FREECAD ASSEMBLY — COMPONENT RECIPES ("MainAssembly")

This assembly document has 21 components, labeled P0..P20 below (a component is one placed body or linked part). 10 of them carry a construction recipe — the FreeCAD feature program that regenerates the part from scratch, quoted from this document or its linked companion documents; the rest are supplied as boundary geometry only. No exploded tour is included for this assembly.
COMPONENT P0 — recipe-attached ("AxleHolderPart", a linked part whose construction recipe lives in a companion FreeCAD document of the same project; that document's serialized recipe follows).
Construction recipe (the companion document, serialized — sketch geometry with constraints, then the solid features built on it; lengths are millimeters unless a unit is written):

FCSTD DOCUMENT  (FreeCAD 1.0R39109 (Git))
Label: AxleHolder
License: All rights reserved
LicenseURL: https://en.wikipedia.org/wiki/All_rights_reserved
objects: Sketcher::SketchObject×2, PartDesign::Pad×2, PartDesign::Body×1, App::Part×1
note: 11 computed .brp shape members not serialized (recipe doc carries the construction recipe); baked Part::Feature solids carry a one-line shape summary decoded from their .brp

FEATURE [Sketcher::SketchObject] Sketch
  ArcFitTolerance = 1e-06
  AttachmentSupport = -> [XY_Plane001]
  FullyConstrained = true
  MakeInternals = false
  MapMode = 5
  sketch-geometry (6):
    g0: LineSegment StartX=-7.3 StartY=-4.3 StartZ=0 EndX=7.3 EndY=-4.3 EndZ=0
    g1: LineSegment StartX=7.3 StartY=-4.3 StartZ=0 EndX=7.3 EndY=4.3 EndZ=0
    g2: LineSegment StartX=7.3 StartY=4.3 StartZ=0 EndX=-7.3 EndY=4.3 EndZ=0
    g3: LineSegment StartX=-7.3 StartY=4.3 StartZ=0 EndX=-7.3 EndY=-4.3 EndZ=0
    g4: GeomPoint [constr] X=0 Y=0 Z=0
    g5: Circle CenterX=0 CenterY=0 CenterZ=0 NormalX=0 NormalY=0 NormalZ=1 AngleXU=0 Radius=3.2
  constraints (14):
    c: Coincident(g0,g1)
    c: Coincident(g1,g2)
    c: Coincident(g2,g3)
    c: Coincident(g3,g0)
    c: Horizontal(g0)
    c: Horizontal(g2)
    c: Vertical(g1)
    c: Vertical(g3)
    c: Symmetric(g2,g0,g4)
    c: Distance(g1,g3) = 14.6
    c: Distance(g0,g2) = 8.6
    c: Coincident(g4,g-1)
    c: Diameter(g5) = 6.4
    c: Coincident(g5,g4)
FEATURE [PartDesign::Pad] Pad
  Direction = (0,0,1)
  Length = 2.6
  Length2 = 10
  Profile = -> Sketch
  ReferenceAxis = -> Sketch [N_Axis]
  Refine = true
  Suppressed = false
  Type = 0
FEATURE [Sketcher::SketchObject] Sketch001
  ArcFitTolerance = 1e-06
  AttachmentSupport = -> [Pad]
  ExternalGeometry = -> [Sketch]
  FullyConstrained = true
  MakeInternals = false
  MapMode = 5
  Placement = pos=(0,0,2.6) rot=(0,0,1;0rad)
  sketch-geometry (6):
    g0: Circle CenterX=0 CenterY=0 CenterZ=0 NormalX=0 NormalY=0 NormalZ=1 AngleXU=0 Radius=3.2
    g1: LineSegment StartX=-4.3 StartY=-4.3 StartZ=0 EndX=4.3 EndY=-4.3 EndZ=0
    g2: LineSegment StartX=4.3 StartY=-4.3 StartZ=0 EndX=4.3 EndY=4.3 EndZ=0
    g3: LineSegment StartX=4.3 StartY=4.3 StartZ=0 EndX=-4.3 EndY=4.3 EndZ=0
    g4: LineSegment StartX=-4.3 StartY=4.3 StartZ=0 EndX=-4.3 EndY=-4.3 EndZ=0
    g5: GeomPoint [constr] X=0 Y=0 Z=0
  constraints (14):
    c: Coincident(g0,g-1)
    c: Equal(g0,g-3)
    c: Coincident(g1,g2)
    c: Coincident(g2,g3)
    c: Coincident(g3,g4)
    c: Coincident(g4,g1)
    c: Horizontal(g1)
    c: Horizontal(g3)
    c: Vertical(g2)
    c: Vertical(g4)
    c: Symmetric(g3,g1,g5)
    c: Coincident(g5,g0)
    c: PointOnObject(g2,g-4)
    c: Equal(g3,g2)
FEATURE [PartDesign::Pad] Pad001
  BaseFeature = -> Pad
  Direction = (0,0,1)
  Length = 4.4
  Length2 = 10
  Profile = -> Sketch001
  ReferenceAxis = -> Sketch001 [N_Axis]
  Refine = true
  Suppressed = false
  Type = 0
FEATURE [PartDesign::Body] Body  label="AxleHolderBody"
  AllowCompound = false
  Group = -> [Sketch,Pad,Sketch001,Pad001]
  Origin = -> Origin001
  Tip = -> Pad001
FEATURE [App::Part] Part  label="AxleHolderPart"
  Group = -> [Body]
  Origin = -> Origin
COMPONENT P1 — same part as P0; its construction recipe is shown at P0.
COMPONENT P2 — same part as P0; its construction recipe is shown at P0.
COMPONENT P3 — geometry summary ("BackWheelAxlePart"; no construction recipe available for this part):
  bounding box: 39.9 x 14.0 x 14.0 mm
  tessellated surface: 2,774 triangles
  volume: 1874 mm^3 (24% of its bounding box)
  symmetry: 2-fold rotationally symmetric about the x axis
COMPONENT P4 — geometry summary ("BackWheelAxlePart001"; no construction recipe available for this part):
  bounding box: 39.9 x 14.0 x 14.0 mm
  tessellated surface: 2,774 triangles
  volume: 1874 mm^3 (24% of its bounding box)
  symmetry: 2-fold rotationally symmetric about the x axis
COMPONENT P5 — geometry summary ("BackWheelConnectorPart"; no construction recipe available for this part):
  bounding box: 23.7 x 23.7 x 20.0 mm
  tessellated surface: 5,512 triangles
  volume: 2183 mm^3 (19% of its bounding box)
COMPONENT P6 — geometry summary ("BackWheelConnectorPart001"; no construction recipe available for this part):
  bounding box: 23.7 x 23.7 x 20.0 mm
  tessellated surface: 5,512 triangles
  volume: 2183 mm^3 (19% of its bounding box)
COMPONENT P7 — geometry summary ("BackWheelStopperPart"; no construction recipe available for this part):
  bounding box: 28.0 x 15.0 x 3.6 mm
  tessellated surface: 2,928 triangles
  volume: 623 mm^3 (41% of its bounding box)
  symmetry: 2-fold rotationally symmetric about the x axis; mirror-symmetric across its y mid-plane, z mid-plane
COMPONENT P8 — geometry summary ("BackWheelStopperPart001"; no construction recipe available for this part):
  bounding box: 28.0 x 15.0 x 3.6 mm
  tessellated surface: 2,928 triangles
  volume: 623 mm^3 (41% of its bounding box)
  symmetry: 2-fold rotationally symmetric about the x axis; mirror-symmetric across its y mid-plane, z mid-plane
COMPONENT P9 — recipe-attached ("ChassisPart", a linked part whose construction recipe lives in a companion FreeCAD document of the same project; that document's serialized recipe follows).
Construction recipe (the companion document, serialized — sketch geometry with constraints, then the solid features built on it; lengths are millimeters unless a unit is written):

FCSTD DOCUMENT  (FreeCAD 1.0R39319 (Git))
Label: Chassis
License: All rights reserved
LicenseURL: https://en.wikipedia.org/wiki/All_rights_reserved
objects: Sketcher::SketchObject×18, PartDesign::Pocket×11, PartDesign::Pad×7, PartDesign::Fillet×2, App::Link×1, PartDesign::SubShapeBinder×1, PartDesign::Body×1, App::Part×1
note: 98 computed .brp shape members not serialized (recipe doc carries the construction recipe); baked Part::Feature solids carry a one-line shape summary decoded from their .brp
EXTERNAL_REF file=../Models/SteeringAckermannModel.FCStd obj=Spreadsheet
EXTERNAL_REF file=../Models/SteeringAckermannModel.FCStd obj=Part

FEATURE [App::Link] Link  label="SteeringAckermannSpreadsheet"
  LinkedObject = -> <external ../Models/SteeringAckermannModel.FCStd>#Spreadsheet
FEATURE [PartDesign::SubShapeBinder] Binder  label="SteeringAckermannModel"
  BindCopyOnChange = 0
  BindMode = 0
  ClaimChildren = false
  Context = -> Part [Body.Binder.]
  Fuse = false
  MakeFace = true
  OffsetFill = false
  OffsetIntersection = false
  OffsetJoinType = 0
  OffsetOpenResult = false
  PartialLoad = false
  Refine = true
  Relative = true
  Support = -> [<external ../Models/SteeringAckermannModel.FCStd>#Part[Sketch001.]]
  _Version = 2
FEATURE [Sketcher::SketchObject] Sketch
  ArcFitTolerance = 1e-06
  AttachmentSupport = -> [XY_Plane001]
  ExternalGeometry = -> [Binder]
  FullyConstrained = true
  MakeInternals = false
  MapMode = 5
  expr: Constraints[31] = <<SteeringAckermannSpreadsheet>>.wheeldepth / 2 + 4
  expr: Constraints[33] = <<SteeringAckermannSpreadsheet>>.wheeldia / 2 + 2
  expr: Constraints[34] = <<SteeringAckermannSpreadsheet>>.wheeldia / 2
  expr: Constraints[43] = <<SteeringAckermannSpreadsheet>>.bodywidth
  sketch-geometry (22):
    g0: LineSegment StartX=-26 StartY=4 StartZ=0 EndX=-26 EndY=-4 EndZ=0
    g1: LineSegment StartX=-26 StartY=4 StartZ=0 EndX=-10 EndY=22 EndZ=0
    g2: LineSegment StartX=-10 StartY=22 StartZ=0 EndX=10 EndY=22 EndZ=0
    g3: LineSegment StartX=-26 StartY=-4 StartZ=0 EndX=-14 EndY=-13 EndZ=0
    g4: LineSegment StartX=-14 StartY=-13 StartZ=0 EndX=-14 EndY=-41 EndZ=0
    g5: LineSegment StartX=10 StartY=22 StartZ=0 EndX=26 EndY=4 EndZ=0
    g6: LineSegment StartX=26 StartY=4 StartZ=0 EndX=26 EndY=-4 EndZ=0
    g7: LineSegment StartX=26 StartY=-4 StartZ=0 EndX=14 EndY=-13 EndZ=0
    g8: LineSegment StartX=14 StartY=-13 StartZ=0 EndX=14 EndY=-41 EndZ=0
    g9: LineSegment StartX=-14 StartY=-41 StartZ=0 EndX=-60 EndY=-41 EndZ=0
    g10: LineSegment StartX=-60 StartY=-41 StartZ=0 EndX=-60 EndY=-164 EndZ=0
    g11: LineSegment StartX=-60 StartY=-164 StartZ=0 EndX=-32 EndY=-164 EndZ=0
    g12: LineSegment StartX=-32 StartY=-164 StartZ=0 EndX=-32 EndY=-222 EndZ=0
    g13: LineSegment StartX=-32 StartY=-222 StartZ=0 EndX=32 EndY=-222 EndZ=0
    g14: LineSegment StartX=14 StartY=-41 StartZ=0 EndX=60 EndY=-41 EndZ=0
    g15: LineSegment StartX=60 StartY=-41 StartZ=0 EndX=60 EndY=-164 EndZ=0
    g16: LineSegment StartX=60 StartY=-164 StartZ=0 EndX=32 EndY=-164 EndZ=0
    g17: LineSegment StartX=32 StartY=-164 StartZ=0 EndX=32 EndY=-222 EndZ=0
    g18: Circle CenterX=-22 CenterY=0 CenterZ=0 NormalX=0 NormalY=0 NormalZ=1 AngleXU=0 Radius=1.5
    g19: Circle CenterX=22 CenterY=0 CenterZ=0 NormalX=0 NormalY=0 NormalZ=1 AngleXU=0 Radius=1.5
    g20: Circle CenterX=-11.3195 CenterY=16 CenterZ=0 NormalX=0 NormalY=0 NormalZ=1 AngleXU=0 Radius=1.5
    g21: Circle CenterX=11.3195 CenterY=16 CenterZ=0 NormalX=0 NormalY=0 NormalZ=1 AngleXU=0 Radius=1.5
  constraints (54):
    c: Distance(g0,g0) = 8
    c: Symmetric(g0,g0,g-1)
    c: Distance(g-3,g0) = 8
    c: Coincident(g1,g0)
    c: Coincident(g2,g1)
    c: DistanceX(g2,g2) = 20
    c: Distance(g-1,g2) = 22
    c: Symmetric(g1,g2,g-2)
    c: Coincident(g3,g0)
    c: Coincident(g4,g3)
    c: Vertical(g4)
    c: DistanceY(g4,g4) = 28
    c: Coincident(g5,g2)
    c: Coincident(g6,g5)
    c: Coincident(g7,g6)
    c: Coincident(g8,g7)
    c: Symmetric(g0,g5,g-2)
    c: Symmetric(g0,g6,g-2)
    c: Symmetric(g3,g7,g-2)
    c: Symmetric(g4,g8,g-2)
    c: Distance(g8,g4) = 28
    c: Coincident(g9,g4)
    c: Horizontal(g9)
    c: Coincident(g10,g9)
    c: Vertical(g10)
    c: Coincident(g11,g10)
    c: Horizontal(g11)
    c: Coincident(g12,g11)
    c: Vertical(g12)
    c: Coincident(g13,g12)
    c: DistanceY(g10,g10) = 123
    c: Distance(g-5,g12) = 16
    c: Symmetric(g12,g13,g-2)
    c: DistanceY(g-7,g11) = 30
    c: DistanceY(g12,g-7) = 28
    c: Coincident(g14,g8)
    c: Coincident(g15,g14)
    c: Coincident(g16,g15)
    c: Coincident(g17,g16)
    c: Coincident(g17,g13)
    c: Symmetric(g9,g14,g-2)
    c: Symmetric(g10,g15,g-2)
    c: Symmetric(g11,g16,g-2)
    c: Distance(g15,g10) = 120
    c: Diameter(g18) = 3
    c: PointOnObject(g18,g-1)
    c: Distance(g18,g0) = 4
    c: Symmetric(g18,g19,g-2)
    c: Diameter(g20) = 3
    c: Equal(g18,g19)
    c: Distance(g20,g1) = 3
    c: DistanceY(g20,g1) = 6
    c: Symmetric(g20,g21,g-2)
    c: Equal(g20,g21)
FEATURE [PartDesign::Pad] Pad
  Direction = (0,0,1)
  Length = 8
  Length2 = 10
  Profile = -> Sketch
  ReferenceAxis = -> Sketch [N_Axis]
  Refine = true
  Suppressed = false
  Type = 0
FEATURE [Sketcher::SketchObject] Sketch001
  ArcFitTolerance = 1e-06
  AttachmentSupport = -> [Pad]
  ExternalGeometry = -> [Sketch]
  FullyConstrained = true
  MakeInternals = false
  MapMode = 5
  Placement = pos=(0,0,8) rot=(0,0,1;0rad)
  sketch-geometry (16):
    g0: LineSegment StartX=-26 StartY=-4 StartZ=0 EndX=-26 EndY=4 EndZ=0
    g1: LineSegment StartX=-26 StartY=4 StartZ=0 EndX=-10 EndY=22 EndZ=0
    g2: LineSegment StartX=10 StartY=22 StartZ=0 EndX=26 EndY=4 EndZ=0
    g3: LineSegment StartX=26 StartY=4 StartZ=0 EndX=26 EndY=-4 EndZ=0
    g4: Circle CenterX=-22 CenterY=0 CenterZ=0 NormalX=0 NormalY=0 NormalZ=1 AngleXU=0 Radius=1.5
    g5: Circle CenterX=-11.3195 CenterY=16 CenterZ=0 NormalX=0 NormalY=0 NormalZ=1 AngleXU=0 Radius=1.5
    g6: Circle CenterX=11.3195 CenterY=16 CenterZ=0 NormalX=0 NormalY=0 NormalZ=1 AngleXU=0 Radius=1.5
    g7: Circle CenterX=22 CenterY=0 CenterZ=0 NormalX=0 NormalY=0 NormalZ=1 AngleXU=0 Radius=1.5
    g8: LineSegment StartX=-10 StartY=22 StartZ=0 EndX=-8 EndY=22 EndZ=0
    g9: LineSegment StartX=-26 StartY=-4 StartZ=0 EndX=-11.3 EndY=-4 EndZ=0
    g10: LineSegment StartX=-11.3 StartY=-4 StartZ=0 EndX=-8 EndY=-2.75 EndZ=0
    g11: LineSegment StartX=-8 StartY=22 StartZ=0 EndX=-8 EndY=-2.75 EndZ=0
    g12: LineSegment StartX=10 StartY=22 StartZ=0 EndX=8 EndY=22 EndZ=0
    g13: LineSegment StartX=8 StartY=22 StartZ=0 EndX=8 EndY=-2.75 EndZ=0
    g14: LineSegment StartX=8 StartY=-2.75 StartZ=0 EndX=11.3 EndY=-4 EndZ=0
    g15: LineSegment StartX=11.3 StartY=-4 StartZ=0 EndX=26 EndY=-4 EndZ=0
  constraints (35):
    c: Coincident(g0,g-4)
    c: Coincident(g0,g-5)
    c: Coincident(g1,g0)
    c: Coincident(g1,g-6)
    c: Coincident(g2,g-8)
    c: Coincident(g3,g2)
    c: Coincident(g3,g-8)
    c: Coincident(g4,g-3)
    c: Equal(g4,g-3)
    c: Coincident(g5,g-9)
    c: Equal(g5,g-9)
    c: Coincident(g6,g-10)
    c: Equal(g6,g-10)
    c: Coincident(g7,g-11)
    c: Equal(g7,g-11)
    c: Coincident(g2,g-7)
    c: Coincident(g8,g1)
    c: PointOnObject(g8,g-6)
    c: Coincident(g9,g0)
    c: Horizontal(g9)
    c: Coincident(g10,g9)
    c: Coincident(g11,g8)
    c: Coincident(g11,g10)
    c: Vertical(g11)
    c: DistanceY(g11,g11) = 24.75
    c: DistanceX(g9,g9) = 14.7
    c: Coincident(g12,g2)
    c: Coincident(g13,g12)
    c: Coincident(g14,g13)
    c: Coincident(g15,g14)
    c: Coincident(g15,g3)
    c: Symmetric(g8,g12,g-2)
    c: Symmetric(g10,g13,g-2)
    c: Symmetric(g9,g14,g-2)
    c: DistanceX(g10,g13) = 16
FEATURE [PartDesign::Pad] Pad001
  BaseFeature = -> Pad
  Direction = (0,0,1)
  Length = 5.5
  Length2 = 10
  Profile = -> Sketch001
  ReferenceAxis = -> Sketch001 [N_Axis]
  Refine = true
  Suppressed = false
  Type = 0
  expr: Length = <<SteeringAckermannSpreadsheet>>.wheeldia / 2 - 8 - 8 - 3 - 7 / 2
FEATURE [Sketcher::SketchObject] Sketch002
  ArcFitTolerance = 1e-06
  AttachmentSupport = -> [Pad001]
  ExternalGeometry = -> [Sketch001,Binder]
  FullyConstrained = true
  MakeInternals = false
  MapMode = 5
  Placement = pos=(0,0,13.5) rot=(0,0,1;0rad)
  sketch-geometry (22):
    g0: LineSegment StartX=-26 StartY=4 StartZ=0 EndX=-10 EndY=22 EndZ=0
    g1: LineSegment StartX=-10 StartY=22 StartZ=0 EndX=-8 EndY=22 EndZ=0
    g2: LineSegment StartX=-8 StartY=22 StartZ=0 EndX=-8 EndY=-2.75 EndZ=0
    g3: LineSegment StartX=-8 StartY=-2.75 StartZ=0 EndX=-11.3 EndY=-4 EndZ=0
    g4: LineSegment StartX=-11.3 StartY=-4 StartZ=0 EndX=-26 EndY=-4 EndZ=0
    g5: LineSegment StartX=26 StartY=4 StartZ=0 EndX=10 EndY=22 EndZ=0
    g6: LineSegment StartX=10 StartY=22 StartZ=0 EndX=8 EndY=22 EndZ=0
    g7: LineSegment StartX=8 StartY=22 StartZ=0 EndX=8 EndY=-2.75 EndZ=0
    g8: LineSegment StartX=8 StartY=-2.75 StartZ=0 EndX=11.3 EndY=-4 EndZ=0
    g9: LineSegment StartX=11.3 StartY=-4 StartZ=0 EndX=26 EndY=-4 EndZ=0
    g10: Circle CenterX=-22 CenterY=0 CenterZ=0 NormalX=0 NormalY=0 NormalZ=1 AngleXU=0 Radius=1.5
    g11: Circle CenterX=-11.3195 CenterY=16 CenterZ=0 NormalX=0 NormalY=0 NormalZ=1 AngleXU=0 Radius=1.5
    g12: Circle CenterX=22 CenterY=0 CenterZ=0 NormalX=0 NormalY=0 NormalZ=1 AngleXU=0 Radius=1.5
    g13: Circle CenterX=11.3195 CenterY=16 CenterZ=0 NormalX=0 NormalY=0 NormalZ=1 AngleXU=0 Radius=1.5
    g14: Circle CenterX=-34 CenterY=0 CenterZ=0 NormalX=0 NormalY=0 NormalZ=1 AngleXU=0 Radius=1.5
    g15: Circle CenterX=34 CenterY=0 CenterZ=0 NormalX=0 NormalY=0 NormalZ=1 AngleXU=0 Radius=1.5
    g16: ArcOfCircle CenterX=-34 CenterY=0 CenterZ=0 NormalX=0 NormalY=0 NormalZ=1 AngleXU=0 Radius=4 StartAngle=1.5708 EndAngle=4.71239
    g17: LineSegment StartX=-26 StartY=-4 StartZ=0 EndX=-34 EndY=-4 EndZ=0
    g18: LineSegment StartX=-26 StartY=4 StartZ=0 EndX=-34 EndY=4 EndZ=0
    g19: ArcOfCircle CenterX=34 CenterY=0 CenterZ=0 NormalX=0 NormalY=0 NormalZ=1 AngleXU=0 Radius=4 StartAngle=4.71239 EndAngle=7.85398
    g20: LineSegment StartX=26 StartY=-4 StartZ=0 EndX=34 EndY=-4 EndZ=0
    g21: LineSegment StartX=26 StartY=4 StartZ=0 EndX=34 EndY=4 EndZ=0
  constraints (44):
    c: Coincident(g0,g-3)
    c: Coincident(g0,g-4)
    c: Coincident(g1,g0)
    c: Coincident(g1,g-5)
    c: Coincident(g2,g1)
    c: Coincident(g2,g-6)
    c: Coincident(g3,g2)
    c: Coincident(g3,g-7)
    c: Coincident(g4,g3)
    c: Coincident(g4,g-7)
    c: Coincident(g5,g-12)
    c: Coincident(g5,g-12)
    c: Coincident(g6,g5)
    c: Coincident(g6,g-11)
    c: Coincident(g7,g6)
    c: Coincident(g7,g-13)
    c: Coincident(g8,g7)
    c: Coincident(g8,g-14)
    c: Coincident(g9,g8)
    c: Coincident(g9,g-14)
    c: Coincident(g10,g-8)
    c: Equal(g10,g-8)
    c: Coincident(g11,g-9)
    c: Equal(g11,g-9)
    c: Coincident(g12,g-15)
    c: Equal(g12,g-15)
    c: Coincident(g13,g-16)
    c: Equal(g13,g-16)
    c: Diameter(g14) = 3
    c: Coincident(g14,g-17)
    c: Coincident(g15,g-18)
    c: Equal(g14,g15)
    c: Coincident(g16,g14)
    c: Coincident(g17,g4)
    c: Coincident(g18,g0)
    c: Tangent(g18,g16) = -1.5708
    c: Tangent(g17,g16) = 1.5708
    c: Horizontal(g17)
    c: Coincident(g19,g15)
    c: Coincident(g20,g9)
    c: Coincident(g21,g5)
    c: Tangent(g20,g19) = -1.5708
    c: Tangent(g21,g19) = 1.5708
    c: Horizontal(g20)
FEATURE [PartDesign::Pad] Pad002
  BaseFeature = -> Pad001
  Direction = (0,0,1)
  Length = 3
  Length2 = 10
  Profile = -> Sketch002
  ReferenceAxis = -> Sketch002 [N_Axis]
  Refine = true
  Suppressed = false
  Type = 0
FEATURE [Sketcher::SketchObject] Sketch003
  ArcFitTolerance = 1e-06
  AttachmentSupport = -> [Pad002]
  ExternalGeometry = -> [Sketch]
  FullyConstrained = true
  MakeInternals = false
  MapMode = 5
  Placement = pos=(0,0,16.5) rot=(0,0,1;0rad)
  expr: Constraints[24] = Sketch001.Constraints[24]
  expr: Constraints[25] = Sketch001.Constraints[25]
  expr: Constraints[34] = Sketch001.Constraints[34]
  sketch-geometry (16):
    g0: LineSegment StartX=-26 StartY=-4 StartZ=0 EndX=-26 EndY=4 EndZ=0
    g1: LineSegment StartX=-26 StartY=4 StartZ=0 EndX=-10 EndY=22 EndZ=0
    g2: LineSegment StartX=10 StartY=22 StartZ=0 EndX=26 EndY=4 EndZ=0
    g3: LineSegment StartX=26 StartY=4 StartZ=0 EndX=26 EndY=-4 EndZ=0
    g4: Circle CenterX=-22 CenterY=0 CenterZ=0 NormalX=0 NormalY=0 NormalZ=1 AngleXU=0 Radius=1.5
    g5: Circle CenterX=-11.3195 CenterY=16 CenterZ=0 NormalX=0 NormalY=0 NormalZ=1 AngleXU=0 Radius=1.5
    g6: Circle CenterX=11.3195 CenterY=16 CenterZ=0 NormalX=0 NormalY=0 NormalZ=1 AngleXU=0 Radius=1.5
    g7: Circle CenterX=22 CenterY=0 CenterZ=0 NormalX=0 NormalY=0 NormalZ=1 AngleXU=0 Radius=1.5
    g8: LineSegment StartX=-10 StartY=22 StartZ=0 EndX=-8 EndY=22 EndZ=0
    g9: LineSegment StartX=-26 StartY=-4 StartZ=0 EndX=-11.3 EndY=-4 EndZ=0
    g10: LineSegment StartX=-11.3 StartY=-4 StartZ=0 EndX=-8 EndY=-2.75 EndZ=0
    g11: LineSegment StartX=-8 StartY=22 StartZ=0 EndX=-8 EndY=-2.75 EndZ=0
    g12: LineSegment StartX=10 StartY=22 StartZ=0 EndX=8 EndY=22 EndZ=0
    g13: LineSegment StartX=8 StartY=22 StartZ=0 EndX=8 EndY=-2.75 EndZ=0
    g14: LineSegment StartX=8 StartY=-2.75 StartZ=0 EndX=11.3 EndY=-4 EndZ=0
    g15: LineSegment StartX=11.3 StartY=-4 StartZ=0 EndX=26 EndY=-4 EndZ=0
  constraints (35):
    c: Coincident(g0,g-4)
    c: Coincident(g0,g-5)
    c: Coincident(g1,g0)
    c: Coincident(g1,g-6)
    c: Coincident(g2,g-8)
    c: Coincident(g3,g2)
    c: Coincident(g3,g-8)
    c: Coincident(g4,g-3)
    c: Equal(g4,g-3)
    c: Coincident(g5,g-9)
    c: Equal(g5,g-9)
    c: Coincident(g6,g-10)
    c: Equal(g6,g-10)
    c: Coincident(g7,g-11)
    c: Equal(g7,g-11)
    c: Coincident(g2,g-7)
    c: Coincident(g8,g1)
    c: PointOnObject(g8,g-6)
    c: Coincident(g9,g0)
    c: Horizontal(g9)
    c: Coincident(g10,g9)
    c: Coincident(g11,g8)
    c: Coincident(g11,g10)
    c: Vertical(g11)
    c: DistanceY(g11,g11) = 24.75
    c: DistanceX(g9,g9) = 14.7
    c: Coincident(g12,g2)
    c: Coincident(g13,g12)
    c: Coincident(g14,g13)
    c: Coincident(g15,g14)
    c: Coincident(g15,g3)
    c: Symmetric(g8,g12,g-2)
    c: Symmetric(g10,g13,g-2)
    c: Symmetric(g9,g14,g-2)
    c: DistanceX(g10,g13) = 16
FEATURE [PartDesign::Pad] Pad003
  BaseFeature = -> Pad002
  Direction = (0,0,1)
  Length = 7
  Length2 = 10
  Profile = -> Sketch003
  ReferenceAxis = -> Sketch003 [N_Axis]
  Refine = true
  Suppressed = false
  Type = 0
FEATURE [Sketcher::SketchObject] Sketch004
  ArcFitTolerance = 1e-06
  AttachmentSupport = -> [Pad003]
  ExternalGeometry = -> [Binder,Pad003]
  FullyConstrained = true
  MakeInternals = false
  MapMode = 5
  Placement = pos=(0,0,8) rot=(0,0,1;0rad)
  sketch-geometry (14):
    g0: LineSegment StartX=-23 StartY=-179 StartZ=0 EndX=-23 EndY=-209 EndZ=0
    g1: LineSegment [constr] StartX=-23 StartY=-209 StartZ=0 EndX=-16 EndY=-209 EndZ=0
    g2: LineSegment StartX=-16 StartY=-209 StartZ=0 EndX=-16 EndY=-179 EndZ=0
    g3: LineSegment StartX=-16 StartY=-179 StartZ=0 EndX=-23 EndY=-179 EndZ=0
    g4: LineSegment StartX=-23 StartY=-222 StartZ=0 EndX=-16 EndY=-222 EndZ=0
    g5: LineSegment StartX=-23 StartY=-222 StartZ=0 EndX=-23 EndY=-209 EndZ=0
    g6: LineSegment StartX=-16 StartY=-222 StartZ=0 EndX=-16 EndY=-209 EndZ=0
    g7: LineSegment StartX=23 StartY=-179 StartZ=0 EndX=23 EndY=-209 EndZ=0
    g8: LineSegment [constr] StartX=23 StartY=-209 StartZ=0 EndX=16 EndY=-209 EndZ=0
    g9: LineSegment StartX=16 StartY=-209 StartZ=0 EndX=16 EndY=-179 EndZ=0
    g10: LineSegment StartX=16 StartY=-179 StartZ=0 EndX=23 EndY=-179 EndZ=0
    g11: LineSegment StartX=23 StartY=-222 StartZ=0 EndX=16 EndY=-222 EndZ=0
    g12: LineSegment StartX=23 StartY=-222 StartZ=0 EndX=23 EndY=-209 EndZ=0
    g13: LineSegment StartX=16 StartY=-222 StartZ=0 EndX=16 EndY=-209 EndZ=0
  constraints (33):
    c: Coincident(g0,g1)
    c: Coincident(g1,g2)
    c: Coincident(g2,g3)
    c: Coincident(g3,g0)
    c: Vertical(g2)
    c: Horizontal(g1)
    c: Horizontal(g3)
    c: Symmetric(g0,g0,g-3)
    c: PointOnObject(g4,g-4)
    c: PointOnObject(g4,g-4)
    c: Coincident(g5,g4)
    c: Coincident(g5,g0)
    c: Vertical(g5)
    c: Coincident(g6,g4)
    c: Coincident(g6,g1)
    c: Vertical(g6)
    c: DistanceY(g0,g0) = 30
    c: DistanceX(g3,g3) = 7
    c: Coincident(g7,g8)
    c: Coincident(g8,g9)
    c: Coincident(g9,g10)
    c: Coincident(g10,g7)
    c: Coincident(g12,g11)
    c: Coincident(g12,g7)
    c: Coincident(g13,g11)
    c: Coincident(g13,g8)
    c: Symmetric(g4,g11,g-2)
    c: Symmetric(g4,g11,g-2)
    c: Symmetric(g1,g8,g-2)
    c: Symmetric(g0,g7,g-2)
    c: Symmetric(g2,g9,g-2)
    c: Symmetric(g0,g7,g-2)
    c: DistanceX(g2,g9) = 32
FEATURE [PartDesign::Pad] Pad004
  BaseFeature = -> Pad003
  Direction = (0,0,1)
  Length = 51
  Length2 = 10
  Profile = -> Sketch004
  ReferenceAxis = -> Sketch004 [N_Axis]
  Refine = true
  Suppressed = false
  Type = 0
FEATURE [Sketcher::SketchObject] Sketch005
  ArcFitTolerance = 1e-06
  AttachmentSupport = -> [Pad004]
  ExternalGeometry = -> [Pad004,Sketch004]
  FullyConstrained = true
  MakeInternals = false
  MapMode = 5
  Placement = pos=(-23,0,0) rot=(0.57735,-0.57735,-0.57735;2.0944rad)
  expr: Constraints[3] = <<SteeringAckermannSpreadsheet>>.wheeldia / 2 - 8 - 8 + 24 / 2
  sketch-geometry (12):
    g0: LineSegment [constr] StartX=194 StartY=59 StartZ=0 EndX=194 EndY=8 EndZ=0
    g1: LineSegment [constr] StartX=179 StartY=32 StartZ=0 EndX=222 EndY=32 EndZ=0
    g2: LineSegment StartX=186.5 StartY=15.5 StartZ=0 EndX=201.5 EndY=15.5 EndZ=0
    g3: LineSegment StartX=201.5 StartY=15.5 StartZ=0 EndX=201.5 EndY=24.5 EndZ=0
    g4: LineSegment StartX=201.5 StartY=24.5 StartZ=0 EndX=186.5 EndY=24.5 EndZ=0
    g5: LineSegment StartX=186.5 StartY=24.5 StartZ=0 EndX=186.5 EndY=15.5 EndZ=0
    g6: GeomPoint [constr] X=194 Y=20 Z=0
    g7: LineSegment StartX=186.5 StartY=48.5 StartZ=0 EndX=201.5 EndY=48.5 EndZ=0
    g8: LineSegment StartX=201.5 StartY=48.5 StartZ=0 EndX=201.5 EndY=39.5 EndZ=0
    g9: LineSegment StartX=201.5 StartY=39.5 StartZ=0 EndX=186.5 EndY=39.5 EndZ=0
    g10: LineSegment StartX=186.5 StartY=39.5 StartZ=0 EndX=186.5 EndY=48.5 EndZ=0
    g11: LineSegment [constr] StartX=209 StartY=8 StartZ=0 EndX=209 EndY=59 EndZ=0
  constraints (30):
    c: PointOnObject(g1,g-5)
    c: PointOnObject(g1,g-6)
    c: Horizontal(g1)
    c: DistanceY(g-5,g1) = 24
    c: Coincident(g2,g3)
    c: Coincident(g3,g4)
    c: Coincident(g4,g5)
    c: Coincident(g5,g2)
    c: Horizontal(g2)
    c: Horizontal(g4)
    c: Vertical(g3)
    c: Vertical(g5)
    c: Symmetric(g4,g2,g6)
    c: PointOnObject(g6,g0)
    c: DistanceX(g2,g2) = 15
    c: DistanceY(g5,g5) = 9
    c: Distance(g6,g1) = 12
    c: Coincident(g7,g8)
    c: Coincident(g8,g9)
    c: Coincident(g9,g10)
    c: Coincident(g10,g7)
    c: Symmetric(g4,g9,g1)
    c: Symmetric(g7,g2,g1)
    c: Symmetric(g8,g3,g1)
    c: Symmetric(g7,g2,g1)
    c: Coincident(g11,g-7)
    c: PointOnObject(g11,g-4)
    c: Vertical(g11)
    c: Symmetric(g-5,g11,g0)
    c: Symmetric(g-5,g11,g0)
FEATURE [PartDesign::Pocket] Pocket
  BaseFeature = -> Pad004
  Direction = (1,0,0)
  Length = 3
  Length2 = 5
  Profile = -> Sketch005
  ReferenceAxis = -> Sketch005 [N_Axis]
  Refine = true
  Suppressed = false
  Type = 0
FEATURE [Sketcher::SketchObject] Sketch006
  ArcFitTolerance = 1e-06
  AttachmentSupport = -> [Pocket]
  ExternalGeometry = -> [Sketch005]
  FullyConstrained = true
  MakeInternals = false
  MapMode = 5
  Placement = pos=(-20,0,0) rot=(0.57735,-0.57735,-0.57735;2.0944rad)
  sketch-geometry (9):
    g0: LineSegment [constr] StartX=194 StartY=15.5 StartZ=0 EndX=194 EndY=48.5 EndZ=0
    g1: LineSegment StartX=189.5 StartY=15.5 StartZ=0 EndX=198.5 EndY=15.5 EndZ=0
    g2: LineSegment StartX=198.5 StartY=15.5 StartZ=0 EndX=198.5 EndY=24.5 EndZ=0
    g3: LineSegment StartX=198.5 StartY=24.5 StartZ=0 EndX=189.5 EndY=24.5 EndZ=0
    g4: LineSegment StartX=189.5 StartY=24.5 StartZ=0 EndX=189.5 EndY=15.5 EndZ=0
    g5: LineSegment StartX=189.5 StartY=48.5 StartZ=0 EndX=189.5 EndY=39.5 EndZ=0
    g6: LineSegment StartX=189.5 StartY=39.5 StartZ=0 EndX=198.5 EndY=39.5 EndZ=0
    g7: LineSegment StartX=198.5 StartY=39.5 StartZ=0 EndX=198.5 EndY=48.5 EndZ=0
    g8: LineSegment StartX=198.5 StartY=48.5 StartZ=0 EndX=189.5 EndY=48.5 EndZ=0
  constraints (24):
    c: Symmetric(g-3,g-3,g0)
    c: Symmetric(g-6,g-6,g0)
    c: Coincident(g1,g2)
    c: Coincident(g2,g3)
    c: Coincident(g3,g4)
    c: Coincident(g4,g1)
    c: Horizontal(g1)
    c: Vertical(g2)
    c: Vertical(g4)
    c: PointOnObject(g1,g-3)
    c: PointOnObject(g2,g-4)
    c: Symmetric(g3,g2,g0)
    c: Equal(g3,g4)
    c: Coincident(g5,g6)
    c: Coincident(g6,g7)
    c: Coincident(g7,g8)
    c: Coincident(g8,g5)
    c: Vertical(g5)
    c: Vertical(g7)
    c: Horizontal(g8)
    c: PointOnObject(g5,g-6)
    c: PointOnObject(g6,g-5)
    c: Symmetric(g5,g6,g0)
    c: Equal(g6,g5)
FEATURE [PartDesign::Pocket] Pocket001
  BaseFeature = -> Pocket
  Direction = (1,0,0)
  Length = 0
  Length2 = 5
  Profile = -> Sketch006
  ReferenceAxis = -> Sketch006 [N_Axis]
  Refine = true
  Suppressed = false
  Type = 3
  UpToFace = -> Pocket [Face35]
FEATURE [Sketcher::SketchObject] Sketch007
  ArcFitTolerance = 1e-06
  AttachmentSupport = -> [Pocket001]
  ExternalGeometry = -> [Sketch005]
  FullyConstrained = true
  MakeInternals = false
  MapMode = 5
  Placement = pos=(-23,0,0) rot=(0.57735,-0.57735,-0.57735;2.0944rad)
  sketch-geometry (6):
    g0: Circle CenterX=183 CenterY=20 CenterZ=0 NormalX=0 NormalY=0 NormalZ=1 AngleXU=0 Radius=1.45
    g1: Circle CenterX=205 CenterY=20 CenterZ=0 NormalX=0 NormalY=0 NormalZ=1 AngleXU=0 Radius=1.45
    g2: LineSegment [constr] StartX=183 StartY=20 StartZ=0 EndX=205 EndY=20 EndZ=0
    g3: GeomPoint X=186.5 Y=20 Z=0
    g4: GeomPoint X=201.5 Y=20 Z=0
    g5: GeomPoint X=194 Y=20 Z=0
  constraints (11):
    c: Diameter(g0) = 2.9
    c: Equal(g0,g1)
    c: Coincident(g2,g0)
    c: Coincident(g2,g1)
    c: Symmetric(g-3,g-3,g2)
    c: PointOnObject(g3,g2)
    c: PointOnObject(g3,g-3)
    c: PointOnObject(g4,g-4)
    c: Symmetric(g3,g4,g5)
    c: Symmetric(g0,g1,g5)
    c: Distance(g0,g-3) = 3.5
FEATURE [PartDesign::Pocket] Pocket002
  BaseFeature = -> Pocket001
  Direction = (1,0,0)
  Length = 0
  Length2 = 5
  Profile = -> Sketch007
  ReferenceAxis = -> Sketch007 [N_Axis]
  Refine = true
  Suppressed = false
  Type = 3
  UpToFace = -> Pocket001 [Face35]
FEATURE [Sketcher::SketchObject] Sketch008
  ArcFitTolerance = 1e-06
  AttachmentSupport = -> [Pocket002]
  ExternalGeometry = -> [Pad004,Sketch004]
  FullyConstrained = true
  MakeInternals = false
  MapMode = 5
  Placement = pos=(23,0,0) rot=(0.57735,0.57735,0.57735;2.0944rad)
  expr: Constraints[14] = Sketch005.Constraints[14]
  expr: Constraints[15] = Sketch005.Constraints[15]
  expr: Constraints[16] = Sketch005.Constraints[16]
  expr: Constraints[3] = Sketch005.Constraints[3]
  sketch-geometry (8):
    g0: LineSegment [constr] StartX=-194 StartY=59 StartZ=0 EndX=-194 EndY=8 EndZ=0
    g1: LineSegment [constr] StartX=-179 StartY=32 StartZ=0 EndX=-222 EndY=32 EndZ=0
    g2: LineSegment StartX=-201.5 StartY=15.5 StartZ=0 EndX=-186.5 EndY=15.5 EndZ=0
    g3: LineSegment StartX=-186.5 StartY=15.5 StartZ=0 EndX=-186.5 EndY=24.5 EndZ=0
    g4: LineSegment StartX=-186.5 StartY=24.5 StartZ=0 EndX=-201.5 EndY=24.5 EndZ=0
    g5: LineSegment StartX=-201.5 StartY=24.5 StartZ=0 EndX=-201.5 EndY=15.5 EndZ=0
    g6: GeomPoint [constr] X=-194 Y=20 Z=0
    g7: LineSegment [constr] StartX=-209 StartY=8 StartZ=0 EndX=-209 EndY=59 EndZ=0
  constraints (22):
    c: PointOnObject(g1,g-5)
    c: PointOnObject(g1,g-6)
    c: Horizontal(g1)
    c: DistanceY(g-5,g1) = 24
    c: Coincident(g2,g3)
    c: Coincident(g3,g4)
    c: Coincident(g4,g5)
    c: Coincident(g5,g2)
    c: Horizontal(g2)
    c: Horizontal(g4)
    c: Vertical(g3)
    c: Vertical(g5)
    c: Symmetric(g4,g2,g6)
    c: PointOnObject(g6,g0)
    c: DistanceX(g2,g2) = 15
    c: DistanceY(g5,g5) = 9
    c: Distance(g6,g1) = 12
    c: Coincident(g7,g-7)
    c: PointOnObject(g7,g-4)
    c: Vertical(g7)
    c: Symmetric(g-5,g7,g0)
    c: Symmetric(g-5,g7,g0)
FEATURE [PartDesign::Pocket] Pocket003
  BaseFeature = -> Pocket002
  Direction = (-1,0,0)
  Length = 3
  Length2 = 5
  Profile = -> Sketch008
  ReferenceAxis = -> Sketch008 [N_Axis]
  Refine = true
  Suppressed = false
  Type = 0
FEATURE [Sketcher::SketchObject] Sketch009
  ArcFitTolerance = 1e-06
  AttachmentSupport = -> [Pocket003]
  ExternalGeometry = -> [Sketch005]
  FullyConstrained = true
  MakeInternals = false
  MapMode = 5
  Placement = pos=(20,0,0) rot=(0.57735,0.57735,0.57735;2.0944rad)
  sketch-geometry (5):
    g0: LineSegment [constr] StartX=-194 StartY=15.5 StartZ=0 EndX=-194 EndY=48.5 EndZ=0
    g1: LineSegment StartX=-198.5 StartY=15.5 StartZ=0 EndX=-189.5 EndY=15.5 EndZ=0
    g2: LineSegment StartX=-189.5 StartY=15.5 StartZ=0 EndX=-189.5 EndY=24.5 EndZ=0
    g3: LineSegment StartX=-189.5 StartY=24.5 StartZ=0 EndX=-198.5 EndY=24.5 EndZ=0
    g4: LineSegment StartX=-198.5 StartY=24.5 StartZ=0 EndX=-198.5 EndY=15.5 EndZ=0
  constraints (13):
    c: Symmetric(g-3,g-3,g0)
    c: Symmetric(g-6,g-6,g0)
    c: Coincident(g1,g2)
    c: Coincident(g2,g3)
    c: Coincident(g3,g4)
    c: Coincident(g4,g1)
    c: Horizontal(g1)
    c: Vertical(g2)
    c: Vertical(g4)
    c: PointOnObject(g1,g-3)
    c: PointOnObject(g2,g-4)
    c: Symmetric(g3,g2,g0)
    c: Equal(g3,g4)
FEATURE [PartDesign::Pocket] Pocket004
  BaseFeature = -> Pocket003
  Direction = (-1,0,0)
  Length = 0
  Length2 = 5
  Profile = -> Sketch009
  ReferenceAxis = -> Sketch009 [N_Axis]
  Refine = true
  Suppressed = false
  Type = 3
  UpToFace = -> Pocket003 [Face34]
FEATURE [Sketcher::SketchObject] Sketch010
  ArcFitTolerance = 1e-06
  AttachmentSupport = -> [Pocket004]
  ExternalGeometry = -> [Sketch005]
  FullyConstrained = true
  MakeInternals = false
  MapMode = 5
  Placement = pos=(23,0,0) rot=(0.57735,0.57735,0.57735;2.0944rad)
  expr: Constraints[0] = Sketch007.Constraints[0]
  expr: Constraints[10] = Sketch007.Constraints[10]
  sketch-geometry (6):
    g0: Circle CenterX=-183 CenterY=20 CenterZ=0 NormalX=0 NormalY=0 NormalZ=1 AngleXU=0 Radius=1.45
    g1: Circle CenterX=-205 CenterY=20 CenterZ=0 NormalX=0 NormalY=0 NormalZ=1 AngleXU=0 Radius=1.45
    g2: LineSegment [constr] StartX=-183 StartY=20 StartZ=0 EndX=-205 EndY=20 EndZ=0
    g3: GeomPoint X=-186.5 Y=20 Z=0
    g4: GeomPoint X=-201.5 Y=20 Z=0
    g5: GeomPoint X=-194 Y=20 Z=0
  constraints (11):
    c: Diameter(g0) = 2.9
    c: Equal(g0,g1)
    c: Coincident(g2,g0)
    c: Coincident(g2,g1)
    c: Symmetric(g-3,g-3,g2)
    c: PointOnObject(g3,g2)
    c: PointOnObject(g3,g-3)
    c: PointOnObject(g4,g-4)
    c: Symmetric(g3,g4,g5)
    c: Symmetric(g0,g1,g5)
    c: Distance(g0,g-3) = 3.5
FEATURE [PartDesign::Pocket] Pocket005
  BaseFeature = -> Pocket004
  Direction = (-1,0,0)
  Length = 0
  Length2 = 5
  Profile = -> Sketch010
  ReferenceAxis = -> Sketch010 [N_Axis]
  Refine = true
  Suppressed = false
  Type = 3
  UpToFace = -> Pocket004 [Face34]
FEATURE [Sketcher::SketchObject] Sketch011
  ArcFitTolerance = 1e-06
  AttachmentSupport = -> [Pocket005]
  ExternalGeometry = -> [Pad004,Sketch004]
  FullyConstrained = true
  MakeInternals = false
  MapMode = 5
  Placement = pos=(23,0,0) rot=(0.57735,0.57735,0.57735;2.0944rad)
  expr: Constraints[3] = Sketch005.Constraints[3]
  sketch-geometry (8):
    g0: LineSegment [constr] StartX=-194 StartY=59 StartZ=0 EndX=-194 EndY=8 EndZ=0
    g1: LineSegment [constr] StartX=-179 StartY=32 StartZ=0 EndX=-222 EndY=32 EndZ=0
    g2: LineSegment [constr] StartX=-209 StartY=8 StartZ=0 EndX=-209 EndY=59 EndZ=0
    g3: GeomPoint X=-194 Y=44 Z=0
    g4: LineSegment StartX=-201.5 StartY=37 StartZ=0 EndX=-186.5 EndY=37 EndZ=0
    g5: LineSegment StartX=-186.5 StartY=37 StartZ=0 EndX=-186.5 EndY=59 EndZ=0
    g6: LineSegment StartX=-186.5 StartY=59 StartZ=0 EndX=-201.5 EndY=59 EndZ=0
    g7: LineSegment StartX=-201.5 StartY=59 StartZ=0 EndX=-201.5 EndY=37 EndZ=0
  constraints (21):
    c: PointOnObject(g1,g-5)
    c: PointOnObject(g1,g-6)
    c: Horizontal(g1)
    c: DistanceY(g-5,g1) = 24
    c: Coincident(g2,g-7)
    c: PointOnObject(g2,g-4)
    c: Vertical(g2)
    c: Symmetric(g-5,g2,g0)
    c: Symmetric(g-5,g2,g0)
    c: PointOnObject(g3,g0)
    c: Distance(g3,g1) = 12
    c: Coincident(g4,g5)
    c: Coincident(g5,g6)
    c: Coincident(g6,g7)
    c: Coincident(g7,g4)
    c: Vertical(g5)
    c: PointOnObject(g5,g-4)
    c: Symmetric(g4,g4,g0)
    c: Symmetric(g5,g6,g0)
    c: DistanceX(g4,g4) = 15
    c: Distance(g3,g4) = 7
FEATURE [PartDesign::Pocket] Pocket006
  BaseFeature = -> Pocket005
  Direction = (-1,0,0)
  Length = 0
  Length2 = 5
  Profile = -> Sketch011
  ReferenceAxis = -> Sketch011 [N_Axis]
  Refine = true
  Suppressed = false
  Type = 3
  UpToFace = -> Pocket005 [Face34]
FEATURE [Sketcher::SketchObject] Sketch012
  ArcFitTolerance = 1e-06
  AttachmentSupport = -> [Pocket006]
  ExternalGeometry = -> [Sketch004]
  FullyConstrained = true
  MakeInternals = false
  MapMode = 5
  Placement = pos=(0,0,59) rot=(0,0,1;0rad)
  sketch-geometry (6):
    g0: Circle CenterX=-19.5 CenterY=-182 CenterZ=0 NormalX=0 NormalY=0 NormalZ=1 AngleXU=0 Radius=1.5
    g1: Circle CenterX=-19.5 CenterY=-219 CenterZ=0 NormalX=0 NormalY=0 NormalZ=1 AngleXU=0 Radius=1.5
    g2: LineSegment [constr] StartX=-19.5 StartY=-179 StartZ=0 EndX=-19.5 EndY=-222 EndZ=0
    g3: GeomPoint X=-19.5 Y=-200.5 Z=0
    g4: Circle CenterX=19.5 CenterY=-182 CenterZ=0 NormalX=0 NormalY=0 NormalZ=1 AngleXU=0 Radius=1.5
    g5: Circle CenterX=19.5 CenterY=-219 CenterZ=0 NormalX=0 NormalY=0 NormalZ=1 AngleXU=0 Radius=1.5
  constraints (12):
    c: Diameter(g0) = 3
    c: Diameter(g1) = 3
    c: Symmetric(g-3,g-3,g2)
    c: Symmetric(g-8,g-8,g2)
    c: PointOnObject(g0,g2)
    c: Symmetric(g2,g2,g3)
    c: Symmetric(g0,g1,g3)
    c: Distance(g0,g-3) = 3
    c: Equal(g0,g4)
    c: Symmetric(g0,g4,g-2)
    c: Equal(g5,g1)
    c: Symmetric(g1,g5,g-2)
FEATURE [PartDesign::Pocket] Pocket007
  BaseFeature = -> Pocket006
  Direction = (0,0,-1)
  Length = 27
  Length2 = 5
  Profile = -> Sketch012
  ReferenceAxis = -> Sketch012 [N_Axis]
  Refine = true
  Suppressed = false
  Type = 0
FEATURE [Sketcher::SketchObject] Sketch013
  ArcFitTolerance = 1e-06
  AttachmentSupport = -> [Pocket007]
  ExternalGeometry = -> [Sketch004]
  FullyConstrained = true
  MakeInternals = false
  MapMode = 5
  Placement = pos=(0,0,8) rot=(0,0,1;0rad)
  sketch-geometry (4):
    g0: LineSegment StartX=16 StartY=-179 StartZ=0 EndX=-16 EndY=-179 EndZ=0
    g1: LineSegment StartX=-16 StartY=-179 StartZ=0 EndX=-16 EndY=-209 EndZ=0
    g2: LineSegment StartX=-16 StartY=-209 StartZ=0 EndX=16 EndY=-209 EndZ=0
    g3: LineSegment StartX=16 StartY=-209 StartZ=0 EndX=16 EndY=-179 EndZ=0
  constraints (10):
    c: Coincident(g0,g1)
    c: Coincident(g1,g2)
    c: Coincident(g2,g3)
    c: Coincident(g3,g0)
    c: Horizontal(g0)
    c: Horizontal(g2)
    c: Vertical(g1)
    c: Vertical(g3)
    c: Coincident(g0,g-4)
    c: Coincident(g1,g-3)
FEATURE [PartDesign::Pocket] Pocket008
  BaseFeature = -> Pocket007
  Direction = (0,0,-1)
  Length = 0
  Length2 = 5
  Profile = -> Sketch013
  ReferenceAxis = -> Sketch013 [N_Axis]
  Refine = true
  Suppressed = false
  Type = 3
  UpToFace = -> Pocket007 [Face4]
FEATURE [Sketcher::SketchObject] Sketch014
  ArcFitTolerance = 1e-06
  AttachmentSupport = -> [Pocket008]
  ExternalGeometry = -> [Pocket008]
  FullyConstrained = true
  MakeInternals = false
  MapMode = 5
  Placement = pos=(0,0,8) rot=(0,0,1;0rad)
  sketch-geometry (17):
    g0: LineSegment StartX=-39 StartY=-90.5 StartZ=0 EndX=-39 EndY=-48.5 EndZ=0
    g1: LineSegment StartX=39 StartY=-48.5 StartZ=0 EndX=39 EndY=-90.5 EndZ=0
    g2: GeomPoint [constr] X=0 Y=-69.5 Z=0
    g3: Circle CenterX=-22.5 CenterY=-94 CenterZ=0 NormalX=0 NormalY=0 NormalZ=1 AngleXU=0 Radius=1.5
    g4: Circle CenterX=35.5 CenterY=-94 CenterZ=0 NormalX=0 NormalY=0 NormalZ=1 AngleXU=0 Radius=1.5
    g5: LineSegment [constr] StartX=-22.5 StartY=-94 StartZ=0 EndX=35.5 EndY=-94 EndZ=0
    g6: Circle CenterX=-22.5 CenterY=-45 CenterZ=0 NormalX=0 NormalY=0 NormalZ=1 AngleXU=0 Radius=1.5
    g7: Circle CenterX=35.5 CenterY=-45 CenterZ=0 NormalX=0 NormalY=0 NormalZ=1 AngleXU=0 Radius=1.5
    g8: LineSegment [constr] StartX=-22.5 StartY=-94 StartZ=0 EndX=-22.5 EndY=-45 EndZ=0
    g9: LineSegment [constr] StartX=-22.5 StartY=-45 StartZ=0 EndX=35.5 EndY=-45 EndZ=0
    g10: LineSegment [constr] StartX=35.5 StartY=-94 StartZ=0 EndX=35.5 EndY=-45 EndZ=0
    g11: LineSegment StartX=-39 StartY=-90.5 StartZ=0 EndX=-15.5 EndY=-90.5 EndZ=0
    g12: LineSegment StartX=-15.5 StartY=-90.5 StartZ=0 EndX=-15.5 EndY=-97.5 EndZ=0
    g13: LineSegment StartX=-15.5 StartY=-97.5 StartZ=0 EndX=5 EndY=-97.5 EndZ=0
    g14: LineSegment StartX=5 StartY=-97.5 StartZ=0 EndX=5 EndY=-90.5 EndZ=0
    g15: LineSegment StartX=5 StartY=-90.5 StartZ=0 EndX=39 EndY=-90.5 EndZ=0
    g16: LineSegment StartX=-39 StartY=-48.5 StartZ=0 EndX=39 EndY=-48.5 EndZ=0
  constraints (45):
    c: Vertical(g0)
    c: Vertical(g1)
    c: Symmetric(g1,g0,g2)
    c: PointOnObject(g2,g-2)
    c: Distance(g0) = 42
    c: Equal(g0,g1)
    c: Diameter(g3) = 3
    c: DistanceY(g3,g0) = 3.5
    c: Equal(g3,g4)
    c: DistanceX(g3,g4) = 58
    c: Coincident(g5,g3)
    c: Coincident(g5,g4)
    c: Horizontal(g5)
    c: Equal(g3,g6)
    c: Equal(g6,g7)
    c: Coincident(g8,g3)
    c: Coincident(g8,g6)
    c: Vertical(g8)
    c: DistanceY(g3,g6) = 49
    c: Coincident(g9,g6)
    c: Coincident(g9,g7)
    c: Horizontal(g9)
    c: Coincident(g10,g4)
    c: Coincident(g10,g7)
    c: Vertical(g10)
    c: Distance(g6,g-3) = 4
    c: Coincident(g11,g0)
    c: Horizontal(g11)
    c: Coincident(g12,g11)
    c: Vertical(g12)
    c: Coincident(g13,g12)
    c: Horizontal(g13)
    c: Coincident(g14,g13)
    c: Vertical(g14)
    c: Coincident(g15,g14)
    c: Coincident(g15,g1)
    c: Horizontal(g15)
    c: DistanceX(g13,g13) = 20.5
    c: Coincident(g16,g0)
    c: Coincident(g16,g1)
    c: Horizontal(g16)
    c: DistanceX(g15,g15) = 34
    c: DistanceY(g12,g12) = 7
    c: DistanceX(g16,g16) = 78
    c: Distance(g0,g8) = 16.5
FEATURE [PartDesign::Pocket] Pocket009
  BaseFeature = -> Pocket008
  Direction = (0,0,-1)
  Length = 0
  Length2 = 5
  Profile = -> Sketch014
  ReferenceAxis = -> Sketch014 [N_Axis]
  Refine = true
  Suppressed = false
  Type = 3
  UpToFace = -> Pocket008 [Face4]
FEATURE [Sketcher::SketchObject] Sketch015
  ArcFitTolerance = 1e-06
  AttachmentSupport = -> [Pocket009]
  ExternalGeometry = -> [Pocket009]
  FullyConstrained = true
  MakeInternals = false
  MapMode = 5
  Placement = pos=(0,0,8) rot=(0,0,1;0rad)
  sketch-geometry (8):
    g0: LineSegment StartX=-25.5 StartY=-122 StartZ=0 EndX=-20.5 EndY=-122 EndZ=0
    g1: LineSegment StartX=-20.5 StartY=-122 StartZ=0 EndX=-20.5 EndY=-134 EndZ=0
    g2: LineSegment StartX=-20.5 StartY=-134 StartZ=0 EndX=-25.5 EndY=-134 EndZ=0
    g3: LineSegment StartX=-25.5 StartY=-134 StartZ=0 EndX=-25.5 EndY=-122 EndZ=0
    g4: LineSegment StartX=20.5 StartY=-122 StartZ=0 EndX=25.5 EndY=-122 EndZ=0
    g5: LineSegment StartX=25.5 StartY=-122 StartZ=0 EndX=25.5 EndY=-134 EndZ=0
    g6: LineSegment StartX=25.5 StartY=-134 StartZ=0 EndX=20.5 EndY=-134 EndZ=0
    g7: LineSegment StartX=20.5 StartY=-134 StartZ=0 EndX=20.5 EndY=-122 EndZ=0
  constraints (22):
    c: Coincident(g0,g1)
    c: Coincident(g1,g2)
    c: Coincident(g2,g3)
    c: Coincident(g3,g0)
    c: Horizontal(g0)
    c: Horizontal(g2)
    c: Vertical(g1)
    c: Vertical(g3)
    c: Distance(g3) = 12
    c: Distance(g0) = 5
    c: Coincident(g4,g5)
    c: Coincident(g5,g6)
    c: Coincident(g6,g7)
    c: Coincident(g7,g4)
    c: Horizontal(g4)
    c: Horizontal(g6)
    c: Vertical(g5)
    c: Vertical(g7)
    c: Symmetric(g0,g4,g-2)
    c: Symmetric(g1,g6,g-2)
    c: Distance(g2,g5) = 51
    c: DistanceY(g-3,g2) = 30
FEATURE [PartDesign::Pad] Pad005
  BaseFeature = -> Pocket009
  Direction = (0,0,1)
  Length = 19
  Length2 = 10
  Profile = -> Sketch015
  ReferenceAxis = -> Sketch015 [N_Axis]
  Refine = true
  Suppressed = false
  Type = 0
FEATURE [Sketcher::SketchObject] Sketch016
  ArcFitTolerance = 1e-06
  AttachmentSupport = -> [Pad005]
  ExternalGeometry = -> [Sketch015]
  FullyConstrained = true
  MakeInternals = false
  MapMode = 5
  Placement = pos=(0,0,27) rot=(0,0,1;0rad)
  sketch-geometry (4):
    g0: LineSegment StartX=25.5 StartY=-122 StartZ=0 EndX=-25.5 EndY=-122 EndZ=0
    g1: LineSegment StartX=-25.5 StartY=-122 StartZ=0 EndX=-25.5 EndY=-134 EndZ=0
    g2: LineSegment StartX=-25.5 StartY=-134 StartZ=0 EndX=25.5 EndY=-134 EndZ=0
    g3: LineSegment StartX=25.5 StartY=-134 StartZ=0 EndX=25.5 EndY=-122 EndZ=0
  constraints (10):
    c: Coincident(g0,g1)
    c: Coincident(g1,g2)
    c: Coincident(g2,g3)
    c: Coincident(g3,g0)
    c: Horizontal(g0)
    c: Horizontal(g2)
    c: Vertical(g1)
    c: Vertical(g3)
    c: Coincident(g0,g-4)
    c: Coincident(g1,g-3)
FEATURE [PartDesign::Pad] Pad006
  BaseFeature = -> Pad005
  Direction = (0,0,1)
  Length = 3
  Length2 = 10
  Profile = -> Sketch016
  ReferenceAxis = -> Sketch016 [N_Axis]
  Refine = true
  Suppressed = false
  Type = 0
FEATURE [Sketcher::SketchObject] Sketch017
  ArcFitTolerance = 1e-06
  AttachmentSupport = -> [Pad006]
  ExternalGeometry = -> [Pad006]
  FullyConstrained = true
  MakeInternals = false
  MapMode = 5
  Placement = pos=(0,0,8) rot=(0,0,1;0rad)
  sketch-geometry (5):
    g0: Circle CenterX=-40 CenterY=-114 CenterZ=0 NormalX=0 NormalY=0 NormalZ=1 AngleXU=0 Radius=1.3
    g1: Circle CenterX=40 CenterY=-114 CenterZ=0 NormalX=0 NormalY=0 NormalZ=1 AngleXU=0 Radius=1.3
    g2: Circle CenterX=-40 CenterY=-157 CenterZ=0 NormalX=0 NormalY=0 NormalZ=1 AngleXU=0 Radius=1.3
    g3: Circle CenterX=40 CenterY=-157 CenterZ=0 NormalX=0 NormalY=0 NormalZ=1 AngleXU=0 Radius=1.3
    g4: LineSegment [constr] StartX=-40 StartY=-114 StartZ=0 EndX=-40 EndY=-157 EndZ=0
  constraints (12):
    c: Diameter(g0) = 2.6
    c: Equal(g0,g1)
    c: Equal(g1,g2)
    c: Equal(g2,g3)
    c: Symmetric(g0,g1,g-2)
    c: Symmetric(g2,g3,g-2)
    c: Coincident(g4,g0)
    c: Coincident(g4,g2)
    c: Vertical(g4)
    c: DistanceX(g0,g1) = 80
    c: DistanceY(g2,g0) = 43
    c: DistanceY(g-3,g2) = 7
FEATURE [PartDesign::Pocket] Pocket010
  BaseFeature = -> Pad006
  Direction = (0,0,-1)
  Length = 0
  Length2 = 5
  Profile = -> Sketch017
  ReferenceAxis = -> Sketch017 [N_Axis]
  Refine = true
  Suppressed = false
  Type = 3
  UpToFace = -> Pad006 [Face6]
FEATURE [PartDesign::Fillet] Fillet
  Base = -> Pocket010 [Edge89,Edge87,Edge81,Edge85]
  BaseFeature = -> Pocket010
  Radius = 1
  Refine = true
  SupportTransform = false
  Suppressed = false
  UseAllEdges = false
FEATURE [PartDesign::Fillet] Fillet001
  Base = -> Fillet [Edge77,Edge111,Edge81,Edge125,Edge85,Edge129,Edge89,Edge134,Edge97,Edge103,Edge192,Edge179]
  BaseFeature = -> Fillet
  Radius = 3
  Refine = true
  SupportTransform = false
  Suppressed = false
  UseAllEdges = false
FEATURE [PartDesign::Body] Body  label="ChassisBody"
  AllowCompound = false
  Group = -> [Binder,Sketch,Pad,Sketch001,Pad001,Sketch002,Pad002,Sketch003,Pad003,Sketch004,Pad004,Sketch005,Pocket,Sketch006,Pocket001,Sketch007,Pocket002,Sketch008,Pocket003,Sketch009,Pocket004,Sketch010,Pocket005,Sketch011,Pocket006,Sketch012,Pocket007,Sketch013,Pocket008,Sketch014,Pocket009,Sketch015,Pad005,Sketch016,Pad006,Sketch017,Pocket010,Fillet,Fillet001]
  Origin = -> Origin001
  Tip = -> Fillet001
FEATURE [App::Part] Part  label="ChassisPart"
  Group = -> [Body]
  Origin = -> Origin
COMPONENT P10 — geometry summary ("LegoBevelGearPart"; no construction recipe available for this part):
  bounding box: 12.9 x 12.8 x 5.2 mm
  tessellated surface: 6,118 triangles
  volume: 226 mm^3 (26% of its bounding box)
COMPONENT P11 — geometry summary ("LegoBevelGearPart001"; no construction recipe available for this part):
  bounding box: 12.8 x 12.8 x 4.0 mm
  tessellated surface: 6,118 triangles
  volume: 226 mm^3 (34% of its bounding box)
  symmetry: 2-fold rotationally symmetric about the x axis
COMPONENT P12 — geometry summary ("LegoBevelGearPart002"; no construction recipe available for this part):
  bounding box: 12.8 x 12.8 x 4.0 mm
  tessellated surface: 6,118 triangles
  volume: 226 mm^3 (34% of its bounding box)
  symmetry: 2-fold rotationally symmetric about the x axis
COMPONENT P13 — geometry summary ("LegoDifferentialGearPart"; no construction recipe available for this part):
  bounding box: 32.0 x 25.8 x 25.8 mm
  tessellated surface: 10,376 triangles
  volume: 2816 mm^3 (13% of its bounding box)
COMPONENT P14 — recipe-attached ("LidarPlatePart", a linked part whose construction recipe lives in a companion FreeCAD document of the same project; that document's serialized recipe follows).
Construction recipe (the companion document, serialized — sketch geometry with constraints, then the solid features built on it; lengths are millimeters unless a unit is written):

FCSTD DOCUMENT  (FreeCAD 1.0R39319 (Git))
Label: LidarPlate
License: All rights reserved
LicenseURL: https://en.wikipedia.org/wiki/All_rights_reserved
objects: Sketcher::SketchObject×2, PartDesign::Pad×2, PartDesign::SubShapeBinder×1, PartDesign::Fillet×1, PartDesign::Body×1, App::Part×1
note: 15 computed .brp shape members not serialized (recipe doc carries the construction recipe); baked Part::Feature solids carry a one-line shape summary decoded from their .brp
EXTERNAL_REF file=Chassis.FCStd obj=Part

FEATURE [PartDesign::SubShapeBinder] Binder
  BindCopyOnChange = 0
  BindMode = 0
  ClaimChildren = false
  Context = -> Part [Body.Binder.]
  Fuse = false
  MakeFace = true
  OffsetFill = false
  OffsetIntersection = false
  OffsetJoinType = 0
  OffsetOpenResult = false
  PartialLoad = false
  Placement = pos=(0,135,0) rot=(0,0,1;0rad)
  Refine = true
  Relative = true
  Support = -> [<external Chassis.FCStd>#Part[Body.Sketch017.]]
  _Version = 2
FEATURE [Sketcher::SketchObject] Sketch
  ArcFitTolerance = 1e-06
  AttachmentSupport = -> [XY_Plane001]
  ExternalGeometry = -> [Binder]
  FullyConstrained = true
  MakeInternals = false
  MapMode = 5
  sketch-geometry (26):
    g0: LineSegment [constr] StartX=-46 StartY=-28 StartZ=0 EndX=46 EndY=-28 EndZ=0
    g1: LineSegment [constr] StartX=46 StartY=-28 StartZ=0 EndX=46 EndY=27 EndZ=0
    g2: LineSegment StartX=46 StartY=27 StartZ=0 EndX=-46 EndY=27 EndZ=0
    g3: LineSegment StartX=-46 StartY=27 StartZ=0 EndX=-46 EndY=-28 EndZ=0
    g4: GeomPoint [constr] X=-1e-15 Y=-0.5 Z=0
    g5: Circle CenterX=20.85 CenterY=15.85 CenterZ=0 NormalX=0 NormalY=0 NormalZ=1 AngleXU=0 Radius=1.5
    g6: Circle CenterX=-20.85 CenterY=-25.85 CenterZ=0 NormalX=0 NormalY=0 NormalZ=1 AngleXU=0 Radius=1.5
    g7: Circle CenterX=20.85 CenterY=-25.85 CenterZ=0 NormalX=0 NormalY=0 NormalZ=1 AngleXU=0 Radius=1.5
    g8: Circle CenterX=-20.85 CenterY=15.85 CenterZ=0 NormalX=0 NormalY=0 NormalZ=1 AngleXU=0 Radius=1.5
    g9: LineSegment [constr] StartX=-20.85 StartY=15.85 StartZ=0 EndX=20.85 EndY=15.85 EndZ=0
    g10: LineSegment [constr] StartX=20.85 StartY=15.85 StartZ=0 EndX=20.85 EndY=-25.85 EndZ=0
    g11: LineSegment [constr] StartX=20.85 StartY=-25.85 StartZ=0 EndX=-20.85 EndY=-25.85 EndZ=0
    g12: LineSegment [constr] StartX=-20.85 StartY=-25.85 StartZ=0 EndX=-20.85 EndY=15.85 EndZ=0
    g13: Circle CenterX=48.85 CenterY=-0.5 CenterZ=0 NormalX=0 NormalY=0 NormalZ=1 AngleXU=0 Radius=6.75
    g14: LineSegment StartX=46 StartY=27 StartZ=0 EndX=60 EndY=27 EndZ=0
    g15: LineSegment StartX=60 StartY=27 StartZ=0 EndX=60 EndY=-28 EndZ=0
    g16: LineSegment [constr] StartX=46 StartY=-28 StartZ=0 EndX=60 EndY=-28 EndZ=0
    g17: LineSegment [constr] StartX=-1e-15 StartY=-0.5 StartZ=0 EndX=60 EndY=-0.5 EndZ=0
    g18: Circle CenterX=-40 CenterY=21 CenterZ=0 NormalX=0 NormalY=0 NormalZ=1 AngleXU=0 Radius=1.5
    g19: Circle CenterX=40 CenterY=21 CenterZ=0 NormalX=0 NormalY=0 NormalZ=1 AngleXU=0 Radius=1.5
    g20: Circle CenterX=-40 CenterY=-22 CenterZ=0 NormalX=0 NormalY=0 NormalZ=1 AngleXU=0 Radius=1.5
    g21: Circle CenterX=40 CenterY=-22 CenterZ=0 NormalX=0 NormalY=0 NormalZ=1 AngleXU=0 Radius=1.5
    g22: GeomPoint X=0 Y=-5 Z=0
    g23: LineSegment StartX=-46 StartY=-28 StartZ=0 EndX=-46 EndY=-32 EndZ=0
    g24: LineSegment StartX=-46 StartY=-32 StartZ=0 EndX=60 EndY=-32 EndZ=0
    g25: LineSegment StartX=60 StartY=-28 StartZ=0 EndX=60 EndY=-32 EndZ=0
  constraints (62):
    c: Coincident(g0,g1)
    c: Coincident(g1,g2)
    c: Coincident(g2,g3)
    c: Coincident(g3,g0)
    c: Horizontal(g0)
    c: Horizontal(g2)
    c: Vertical(g1)
    c: Vertical(g3)
    c: Symmetric(g2,g0,g4)
    c: DistanceX(g0,g0) = 92
    c: DistanceY(g1,g1) = 55
    c: Diameter(g8) = 3
    c: Equal(g8,g5)
    c: Equal(g5,g6)
    c: Equal(g6,g7)
    c: Coincident(g9,g8)
    c: Coincident(g9,g5)
    c: Coincident(g10,g5)
    c: Coincident(g10,g7)
    c: Coincident(g11,g7)
    c: Coincident(g11,g6)
    c: Horizontal(g11)
    c: Coincident(g12,g6)
    c: Coincident(g12,g8)
    c: Horizontal(g9)
    c: Vertical(g10)
    c: Vertical(g12)
    c: Equal(g9,g12)
    c: DistanceX(g9,g9) = 41.7
    c: Diameter(g13) = 13.5
    c: Coincident(g14,g1)
    c: Horizontal(g14)
    c: Coincident(g15,g14)
    c: Vertical(g15)
    c: Coincident(g16,g0)
    c: Coincident(g16,g15)
    c: Horizontal(g16)
    c: DistanceX(g16,g16) = 14
    c: Coincident(g17,g4)
    c: Symmetric(g15,g15,g17)
    c: PointOnObject(g13,g17)
    c: Distance(g13,g10) = 28
    c: Diameter(g18) = 3
    c: Coincident(g18,g-3)
    c: Coincident(g19,g-4)
    c: Coincident(g20,g-5)
    c: Coincident(g21,g-6)
    c: Equal(g18,g19)
    c: Equal(g19,g20)
    c: Equal(g20,g21)
    c: Symmetric(g19,g20,g4)
    c: PointOnObject(g22,g-2)
    c: Symmetric(g6,g5,g22)
    c: DistanceY(g22,g4) = 4.5
    c: Coincident(g23,g0)
    c: Vertical(g23)
    c: Coincident(g24,g23)
    c: Coincident(g25,g15)
    c: Coincident(g25,g24)
    c: Vertical(g25)
    c: Horizontal(g24)
    c: DistanceY(g25,g25) = 4
FEATURE [PartDesign::Pad] Pad
  Direction = (0,0,1)
  Length = 3
  Length2 = 10
  Profile = -> Sketch
  ReferenceAxis = -> Sketch [N_Axis]
  Refine = true
  Suppressed = false
  Type = 0
FEATURE [Sketcher::SketchObject] Sketch001
  ArcFitTolerance = 1e-06
  AttachmentSupport = -> [Pad]
  ExternalGeometry = -> [Sketch]
  FullyConstrained = true
  MakeInternals = false
  MapMode = 5
  Placement = pos=(0,0,0) rot=(1,0,0;3.14159rad)
  sketch-geometry (8):
    g0: Circle CenterX=-40 CenterY=22 CenterZ=0 NormalX=0 NormalY=0 NormalZ=1 AngleXU=0 Radius=4
    g1: Circle CenterX=40 CenterY=22 CenterZ=0 NormalX=0 NormalY=0 NormalZ=1 AngleXU=0 Radius=4
    g2: Circle CenterX=-40 CenterY=-21 CenterZ=0 NormalX=0 NormalY=0 NormalZ=1 AngleXU=0 Radius=4
    g3: Circle CenterX=40 CenterY=-21 CenterZ=0 NormalX=0 NormalY=0 NormalZ=1 AngleXU=0 Radius=4
    g4: Circle CenterX=-40 CenterY=22 CenterZ=0 NormalX=0 NormalY=0 NormalZ=1 AngleXU=0 Radius=1.5
    g5: Circle CenterX=40 CenterY=22 CenterZ=0 NormalX=0 NormalY=0 NormalZ=1 AngleXU=0 Radius=1.5
    g6: Circle CenterX=-40 CenterY=-21 CenterZ=0 NormalX=0 NormalY=0 NormalZ=1 AngleXU=0 Radius=1.5
    g7: Circle CenterX=40 CenterY=-21 CenterZ=0 NormalX=0 NormalY=0 NormalZ=1 AngleXU=0 Radius=1.5
  constraints (16):
    c: Coincident(g0,g-3)
    c: Coincident(g1,g-4)
    c: Coincident(g2,g-5)
    c: Coincident(g3,g-6)
    c: Diameter(g0) = 8
    c: Equal(g0,g1)
    c: Equal(g1,g2)
    c: Equal(g2,g3)
    c: Coincident(g4,g0)
    c: Coincident(g5,g1)
    c: Coincident(g6,g2)
    c: Coincident(g7,g3)
    c: Equal(g-3,g4)
    c: Equal(g5,g-4)
    c: Equal(g6,g-5)
    c: Equal(g7,g-6)
FEATURE [PartDesign::Pad] Pad001
  BaseFeature = -> Pad
  Direction = (0,0,-1)
  Length = 4
  Length2 = 10
  Profile = -> Sketch001
  ReferenceAxis = -> Sketch001 [N_Axis]
  Refine = true
  Suppressed = false
  Type = 0
FEATURE [PartDesign::Fillet] Fillet
  Base = -> Pad001 [Edge5,Edge1,Edge2,Edge9]
  BaseFeature = -> Pad001
  Radius = 2
  Refine = true
  SupportTransform = false
  Suppressed = false
  UseAllEdges = false
FEATURE [PartDesign::Body] Body  label="LidarPlateBody"
  AllowCompound = false
  Group = -> [Binder,Sketch,Pad,Sketch001,Pad001,Fillet]
  Origin = -> Origin001
  Tip = -> Fillet
FEATURE [App::Part] Part  label="LidarPlatePart"
  Group = -> [Body]
  Origin = -> Origin
COMPONENT P15 — recipe-attached ("MotorGearPart", a linked part whose construction recipe lives in a companion FreeCAD document of the same project; that document's serialized recipe follows).
Construction recipe (the companion document, serialized — sketch geometry with constraints, then the solid features built on it; lengths are millimeters unless a unit is written):

FCSTD DOCUMENT  (FreeCAD 1.0R39285 (Git))
Label: MotorGear
License: All rights reserved
LicenseURL: https://en.wikipedia.org/wiki/All_rights_reserved
objects: PartDesign::Pad×3, Sketcher::SketchObject×3, PartDesign::Pocket×2, Part::Feature×1, PartDesign::FeatureBase×1, PartDesign::Chamfer×1, PartDesign::Body×1, App::Part×1
note: 28 computed .brp shape members not serialized (recipe doc carries the construction recipe); baked Part::Feature solids carry a one-line shape summary decoded from their .brp

FEATURE [Part::Feature] Solid  label="Part 1"
  shape: bbox 25.58 x 25.58 x 7.711 mm, 1760 faces (baked)
FEATURE [PartDesign::FeatureBase] BaseFeature
  BaseFeature = -> Solid
  Suppressed = false
FEATURE [PartDesign::Pad] Pad
  AlongSketchNormal = false
  BaseFeature = -> BaseFeature
  Direction = (0,0,1)
  Length = 10
  Length2 = 10
  Profile = -> BaseFeature [Edge322]
  Refine = true
  Suppressed = false
  Type = 3
  UpToFace = -> BaseFeature [Face19]
FEATURE [PartDesign::Pad] Pad001
  AlongSketchNormal = false
  BaseFeature = -> Pad
  Direction = (0,0,1)
  Length = 10
  Length2 = 10
  Profile = -> Pad [Edge1]
  Refine = true
  Suppressed = false
  Type = 3
  UpToFace = -> Pad [Face1545]
FEATURE [Sketcher::SketchObject] Sketch
  ArcFitTolerance = 1e-06
  AttachmentSupport = -> [Pad001]
  FullyConstrained = true
  MakeInternals = false
  MapMode = 5
  Placement = pos=(0,0,-3.85) rot=(1,0,0;3.14159rad)
  sketch-geometry (1):
    g0: Circle CenterX=0 CenterY=0 CenterZ=0 NormalX=0 NormalY=0 NormalZ=1 AngleXU=0 Radius=6
  constraints (2):
    c: Coincident(g0,g-3)
    c: Diameter(g0) = 12
FEATURE [PartDesign::Pocket] Pocket
  BaseFeature = -> Pad001
  Direction = (0,0,1)
  Length = 2
  Length2 = 5
  Profile = -> Sketch
  ReferenceAxis = -> Sketch [N_Axis]
  Refine = true
  Suppressed = false
  Type = 0
FEATURE [Sketcher::SketchObject] Sketch002
  ArcFitTolerance = 1e-06
  AttachmentSupport = -> [Pocket]
  FullyConstrained = true
  MakeInternals = false
  MapMode = 5
  Placement = pos=(0,0,-3.85) rot=(1,0,0;3.14159rad)
  sketch-geometry (1):
    g0: Circle CenterX=0 CenterY=0 CenterZ=0 NormalX=0 NormalY=0 NormalZ=1 AngleXU=0 Radius=3
  constraints (2):
    c: Coincident(g0,g-1)
    c: Diameter(g0) = 6
FEATURE [PartDesign::Pad] Pad004
  AlongSketchNormal = false
  BaseFeature = -> Pocket
  Direction = (0,0,-1)
  Length = 7
  Length2 = 10
  Profile = -> Sketch002
  ReferenceAxis = -> Sketch002 [N_Axis]
  Suppressed = false
  Type = 0
FEATURE [Sketcher::SketchObject] Sketch001
  ArcFitTolerance = 1e-06
  AttachmentSupport = -> [Pad004]
  FullyConstrained = true
  MakeInternals = false
  MapMode = 5
  Placement = pos=(0,0,3.85) rot=(0,0,1;0rad)
  sketch-geometry (5):
    g0: ArcOfCircle CenterX=0 CenterY=0 CenterZ=0 NormalX=0 NormalY=0 NormalZ=1 AngleXU=0 Radius=1.65 StartAngle=5.84506 EndAngle=9.8629
    g1: LineSegment StartX=-0.9 StartY=-1.1 StartZ=0 EndX=0.9 EndY=-1.1 EndZ=0
    g2: ArcOfCircle CenterX=-1.29658 CenterY=-1.0478 CenterZ=0 NormalX=0 NormalY=0 NormalZ=1 AngleXU=0 Radius=0.4 StartAngle=2.08741 EndAngle=6.15231
    g3: ArcOfCircle CenterX=1.29658 CenterY=-1.0478 CenterZ=0 NormalX=0 NormalY=0 NormalZ=1 AngleXU=0 Radius=0.4 StartAngle=3.27247 EndAngle=7.33737
    g4: LineSegment [constr] StartX=-1.49416 StartY=-0.7 StartZ=0 EndX=1.49416 EndY=-0.7 EndZ=0
  constraints (15):
    c: Coincident(g0,g-1)
    c: Diameter(g0) = 3.3
    c: Distance(g0,g1) = 1.1
    c: Coincident(g2,g1)
    c: Coincident(g2,g0)
    c: Coincident(g3,g1)
    c: Coincident(g3,g0)
    c: Equal(g2,g3)
    c: Symmetric(g1,g1,g-2)
    c: Radius(g2) = 0.4
    c: DistanceX(g1,g1) = 1.8
    c: Coincident(g4,g0)
    c: Coincident(g4,g0)
    c: Horizontal(g4)
    c: DistanceY(g1,g0) = 0.4
FEATURE [PartDesign::Pocket] Pocket001
  BaseFeature = -> Pad004
  Direction = (0,0,-1)
  Length = 11
  Length2 = 5
  Profile = -> Sketch001
  ReferenceAxis = -> Sketch001 [N_Axis]
  Refine = true
  Suppressed = false
  Type = 0
FEATURE [PartDesign::Chamfer] Chamfer
  Angle = 60
  Base = -> Pocket001 [Edge4,Edge6,Edge5,Edge7]
  BaseFeature = -> Pocket001
  ChamferType = 2
  FlipDirection = false
  Size = 0.4
  Size2 = 1
  SupportTransform = false
  Suppressed = false
  UseAllEdges = false
FEATURE [PartDesign::Body] Body  label="MotorGearBody"
  AllowCompound = false
  BaseFeature = -> Solid
  Group = -> [BaseFeature,Pad,Pad001,Sketch,Pocket,Pad004,Sketch002,Sketch001,Pocket001,Chamfer]
  Origin = -> Origin
  Tip = -> Chamfer
FEATURE [App::Part] Part  label="MotorGearPart"
  Group = -> [Solid,Body]
  Origin = -> Origin001
COMPONENT P16 — recipe-attached ("MotorHolderPart", a linked part whose construction recipe lives in a companion FreeCAD document of the same project; that document's serialized recipe follows).
Construction recipe (the companion document, serialized — sketch geometry with constraints, then the solid features built on it; lengths are millimeters unless a unit is written):

FCSTD DOCUMENT  (FreeCAD 1.0R39319 (Git))
Label: MotorHolder
License: All rights reserved
LicenseURL: https://en.wikipedia.org/wiki/All_rights_reserved
objects: Sketcher::SketchObject×2, PartDesign::SubShapeBinder×1, PartDesign::Pad×1, PartDesign::Pocket×1, PartDesign::Body×1, App::Part×1
note: 12 computed .brp shape members not serialized (recipe doc carries the construction recipe); baked Part::Feature solids carry a one-line shape summary decoded from their .brp
EXTERNAL_REF file=MotorPlate.FCStd obj=Part

FEATURE [PartDesign::SubShapeBinder] Binder  label="MotorPlateBody"
  BindCopyOnChange = 0
  BindMode = 0
  ClaimChildren = false
  Context = -> Part [Body.Binder.]
  Fuse = false
  MakeFace = true
  OffsetFill = false
  OffsetIntersection = false
  OffsetJoinType = 0
  OffsetOpenResult = false
  PartialLoad = false
  Placement = pos=(-5,0,0) rot=(0,0,1;0rad)
  Refine = true
  Relative = true
  Support = -> [<external MotorPlate.FCStd>#Part[Body.]]
  _Version = 2
FEATURE [Sketcher::SketchObject] Sketch
  ArcFitTolerance = 1e-06
  AttachmentSupport = -> [YZ_Plane001]
  ExternalGeometry = -> [Binder]
  FullyConstrained = true
  MakeInternals = false
  MapMode = 5
  Placement = pos=(0,0,0) rot=(0.57735,0.57735,0.57735;2.0944rad)
  sketch-geometry (13):
    g0: LineSegment StartX=-9 StartY=-15 StartZ=0 EndX=1.8e-15 EndY=-15 EndZ=0
    g1: LineSegment StartX=1.8e-15 StartY=-15 StartZ=0 EndX=1.8e-15 EndY=-25 EndZ=0
    g2: LineSegment StartX=1.8e-15 StartY=-25 StartZ=0 EndX=12 EndY=-25 EndZ=0
    g3: LineSegment StartX=12 StartY=-25 StartZ=0 EndX=12 EndY=-15 EndZ=0
    g4: LineSegment StartX=12 StartY=-15 StartZ=0 EndX=21 EndY=-15 EndZ=0
    g5: LineSegment [constr] StartX=6 StartY=-15 StartZ=0 EndX=6 EndY=-27 EndZ=0
    g6: LineSegment StartX=-9 StartY=-15 StartZ=0 EndX=-9 EndY=-18 EndZ=0
    g7: LineSegment StartX=-9 StartY=-18 StartZ=0 EndX=-2 EndY=-18 EndZ=0
    g8: LineSegment StartX=-2 StartY=-18 StartZ=0 EndX=-2 EndY=-27 EndZ=0
    g9: LineSegment StartX=-2 StartY=-27 StartZ=0 EndX=14 EndY=-27 EndZ=0
    g10: LineSegment StartX=14 StartY=-27 StartZ=0 EndX=14 EndY=-18 EndZ=0
    g11: LineSegment StartX=14 StartY=-18 StartZ=0 EndX=21 EndY=-18 EndZ=0
    g12: LineSegment StartX=21 StartY=-18 StartZ=0 EndX=21 EndY=-15 EndZ=0
  constraints (32):
    c: Coincident(g0,g-3)
    c: PointOnObject(g0,g-3)
    c: Coincident(g1,g0)
    c: Coincident(g2,g1)
    c: Coincident(g3,g2)
    c: PointOnObject(g3,g-3)
    c: Coincident(g4,g3)
    c: Coincident(g4,g-3)
    c: Symmetric(g-3,g-3,g5)
    c: Symmetric(g0,g3,g5)
    c: Symmetric(g1,g2,g5)
    c: Vertical(g1)
    c: Coincident(g6,g0)
    c: Vertical(g6)
    c: Coincident(g7,g6)
    c: Horizontal(g7)
    c: Coincident(g8,g7)
    c: Vertical(g8)
    c: Coincident(g9,g8)
    c: Coincident(g10,g9)
    c: Coincident(g11,g10)
    c: Coincident(g12,g11)
    c: Coincident(g12,g4)
    c: Symmetric(g6,g11,g5)
    c: Symmetric(g7,g10,g5)
    c: Symmetric(g8,g9,g5)
    c: PointOnObject(g5,g9)
    c: DistanceY(g6,g6) = 3
    c: Distance(g1,g8) = 2
    c: DistanceX(g0,g3) = 12
    c: DistanceY(g8,g1) = 2
    c: DistanceY(g1,g1) = 10
FEATURE [PartDesign::Pad] Pad
  Direction = (1,0,0)
  Length = 10
  Length2 = 10
  Placement = pos=(0,0,0) rot=(1,1,1;2.0944rad)
  Profile = -> Sketch
  ReferenceAxis = -> Sketch [N_Axis]
  Refine = true
  Suppressed = false
  Type = 0
FEATURE [Sketcher::SketchObject] Sketch001
  ArcFitTolerance = 1e-06
  AttachmentSupport = -> [Pad]
  ExternalGeometry = -> [Binder]
  FullyConstrained = true
  MakeInternals = false
  MapMode = 5
  Placement = pos=(1.7e-15,-5e-15,-15) rot=(0,0,-1;1.5708rad)
  sketch-geometry (2):
    g0: Circle CenterX=6 CenterY=5 CenterZ=0 NormalX=0 NormalY=0 NormalZ=1 AngleXU=0 Radius=1.6
    g1: Circle CenterX=-18 CenterY=5 CenterZ=0 NormalX=0 NormalY=0 NormalZ=1 AngleXU=0 Radius=1.6
  constraints (4):
    c: Coincident(g0,g-3)
    c: Coincident(g1,g-4)
    c: Diameter(g1) = 3.2
    c: Equal(g1,g0)
FEATURE [PartDesign::Pocket] Pocket
  BaseFeature = -> Pad
  Direction = (0,0,-1)
  Length = 0
  Length2 = 5
  Placement = pos=(0,0,0) rot=(1,1,1;2.0944rad)
  Profile = -> Sketch001
  ReferenceAxis = -> Sketch001 [N_Axis]
  Refine = true
  Suppressed = false
  Type = 3
  UpToFace = -> Pad [Face11]
FEATURE [PartDesign::Body] Body  label="MotorHolderBody"
  AllowCompound = false
  Group = -> [Binder,Sketch,Pad,Sketch001,Pocket]
  Origin = -> Origin001
  Tip = -> Pocket
FEATURE [App::Part] Part  label="MotorHolderPart"
  Group = -> [Body]
  Origin = -> Origin
COMPONENT P17 — recipe-attached ("MotorPlatePart", a linked part whose construction recipe lives in a companion FreeCAD document of the same project; that document's serialized recipe follows).
Construction recipe (the companion document, serialized — sketch geometry with constraints, then the solid features built on it; lengths are millimeters unless a unit is written):

FCSTD DOCUMENT  (FreeCAD 1.0R39319 (Git))
Label: MotorPlate
License: All rights reserved
LicenseURL: https://en.wikipedia.org/wiki/All_rights_reserved
objects: Sketcher::SketchObject×3, PartDesign::Pad×2, PartDesign::SubShapeBinder×1, PartDesign::Pocket×1, PartDesign::Body×1, App::Part×1
note: 17 computed .brp shape members not serialized (recipe doc carries the construction recipe); baked Part::Feature solids carry a one-line shape summary decoded from their .brp
EXTERNAL_REF file=Chassis.FCStd obj=Part

FEATURE [PartDesign::SubShapeBinder] Binder  label="ChassisBody"
  BindCopyOnChange = 0
  BindMode = 0
  ClaimChildren = false
  Context = -> Part [Body.Binder.]
  Fuse = false
  MakeFace = true
  OffsetFill = false
  OffsetIntersection = false
  OffsetJoinType = 0
  OffsetOpenResult = false
  PartialLoad = false
  Placement = pos=(0,200,0) rot=(0,0,1;0rad)
  Refine = true
  Relative = true
  Support = -> [<external Chassis.FCStd>#Part[Body.]]
  _Version = 2
FEATURE [Sketcher::SketchObject] Sketch
  ArcFitTolerance = 1e-06
  AttachmentSupport = -> [XY_Plane001]
  ExternalGeometry = -> [Binder]
  FullyConstrained = true
  MakeInternals = false
  MapMode = 5
  sketch-geometry (12):
    g0: LineSegment StartX=-23 StartY=21 StartZ=0 EndX=23 EndY=21 EndZ=0
    g1: LineSegment StartX=23 StartY=21 StartZ=0 EndX=23 EndY=13.5 EndZ=0
    g2: LineSegment StartX=23 StartY=13.5 StartZ=0 EndX=16 EndY=13.5 EndZ=0
    g3: LineSegment StartX=16 StartY=13.5 StartZ=0 EndX=16 EndY=-1.5 EndZ=0
    g4: LineSegment StartX=16 StartY=-1.5 StartZ=0 EndX=23 EndY=-1.5 EndZ=0
    g5: LineSegment StartX=23 StartY=-1.5 StartZ=0 EndX=23 EndY=-22 EndZ=0
    g6: LineSegment StartX=23 StartY=-22 StartZ=0 EndX=-23 EndY=-22 EndZ=0
    g7: LineSegment StartX=-23 StartY=-22 StartZ=0 EndX=-23 EndY=21 EndZ=0
    g8: Circle CenterX=-19.5 CenterY=18 CenterZ=0 NormalX=0 NormalY=0 NormalZ=1 AngleXU=0 Radius=1.65
    g9: Circle CenterX=19.5 CenterY=18 CenterZ=0 NormalX=0 NormalY=0 NormalZ=1 AngleXU=0 Radius=1.65
    g10: Circle CenterX=-19.5 CenterY=-19 CenterZ=0 NormalX=0 NormalY=0 NormalZ=1 AngleXU=0 Radius=1.65
    g11: Circle CenterX=19.5 CenterY=-19 CenterZ=0 NormalX=0 NormalY=0 NormalZ=1 AngleXU=0 Radius=1.65
  constraints (24):
    c: Coincident(g0,g-4)
    c: Coincident(g0,g-11)
    c: Coincident(g1,g0)
    c: Coincident(g1,g-12)
    c: Coincident(g2,g1)
    c: Coincident(g2,g-12)
    c: Coincident(g3,g2)
    c: Coincident(g3,g-15)
    c: Coincident(g4,g3)
    c: Coincident(g4,g-16)
    c: Coincident(g5,g4)
    c: Coincident(g5,g-17)
    c: Coincident(g6,g5)
    c: Coincident(g6,g-6)
    c: Coincident(g7,g6)
    c: Coincident(g7,g0)
    c: Coincident(g8,g-8)
    c: Coincident(g9,g-13)
    c: Coincident(g10,g-7)
    c: Coincident(g11,g-18)
    c: Diameter(g9) = 3.3
    c: Equal(g9,g8)
    c: Equal(g8,g10)
    c: Equal(g10,g11)
FEATURE [PartDesign::Pad] Pad
  Direction = (0,0,1)
  Length = 5
  Length2 = 10
  Profile = -> Sketch
  ReferenceAxis = -> Sketch [N_Axis]
  Refine = true
  Reversed = true
  Suppressed = false
  Type = 0
FEATURE [Sketcher::SketchObject] Sketch001
  ArcFitTolerance = 1e-06
  AttachmentSupport = -> [Pad]
  ExternalGeometry = -> [Sketch]
  FullyConstrained = true
  MakeInternals = false
  MapMode = 5
  Placement = pos=(0,0,-5) rot=(1,0,0;3.14159rad)
  sketch-geometry (6):
    g0: LineSegment StartX=15 StartY=9 StartZ=0 EndX=5 EndY=9 EndZ=0
    g1: LineSegment StartX=5 StartY=9 StartZ=0 EndX=5 EndY=-21 EndZ=0
    g2: LineSegment StartX=5 StartY=-21 StartZ=0 EndX=15 EndY=-21 EndZ=0
    g3: LineSegment StartX=15 StartY=-21 StartZ=0 EndX=15 EndY=9 EndZ=0
    g4: GeomPoint [constr] X=10 Y=-6 Z=0
    g5: LineSegment [constr] StartX=16 StartY=-6 StartZ=0 EndX=-23 EndY=-6 EndZ=0
  constraints (16):
    c: Coincident(g0,g1)
    c: Coincident(g1,g2)
    c: Coincident(g2,g3)
    c: Coincident(g3,g0)
    c: Horizontal(g0)
    c: Horizontal(g2)
    c: Vertical(g1)
    c: Vertical(g3)
    c: Symmetric(g2,g0,g4)
    c: PointOnObject(g1,g-3)
    c: Symmetric(g-5,g-5,g5)
    c: PointOnObject(g5,g-4)
    c: Horizontal(g5)
    c: PointOnObject(g4,g5)
    c: DistanceX(g0,g0) = 10
    c: Distance(g0,g-4) = 28
FEATURE [PartDesign::Pad] Pad001
  BaseFeature = -> Pad
  Direction = (0,0,-1)
  Length = 10
  Length2 = 10
  Profile = -> Sketch001
  ReferenceAxis = -> Sketch001 [N_Axis]
  Refine = true
  Suppressed = false
  Type = 0
FEATURE [Sketcher::SketchObject] Sketch002
  ArcFitTolerance = 1e-06
  AttachmentSupport = -> [Pad001]
  ExternalGeometry = -> [Sketch001]
  FullyConstrained = true
  MakeInternals = false
  MapMode = 5
  Placement = pos=(0,0,-15) rot=(1,0,0;3.14159rad)
  sketch-geometry (3):
    g0: LineSegment [constr] StartX=10 StartY=9 StartZ=0 EndX=10 EndY=-21 EndZ=0
    g1: Circle CenterX=10 CenterY=6 CenterZ=0 NormalX=0 NormalY=0 NormalZ=1 AngleXU=0 Radius=1.5
    g2: Circle CenterX=10 CenterY=-18 CenterZ=0 NormalX=0 NormalY=0 NormalZ=1 AngleXU=0 Radius=1.5
  constraints (8):
    c: Symmetric(g-3,g-3,g0)
    c: Symmetric(g-4,g-4,g0)
    c: Diameter(g1) = 3
    c: PointOnObject(g1,g0)
    c: Diameter(g2) = 3
    c: PointOnObject(g2,g0)
    c: Distance(g1,g-3) = 3
    c: Distance(g2,g-4) = 3
FEATURE [PartDesign::Pocket] Pocket
  BaseFeature = -> Pad001
  Direction = (0,0,1)
  Length = 0
  Length2 = 5
  Profile = -> Sketch002
  ReferenceAxis = -> Sketch002 [N_Axis]
  Refine = true
  Suppressed = false
  Type = 3
  UpToFace = -> Pad001 [Face2]
FEATURE [PartDesign::Body] Body  label="MotorPlateBody"
  AllowCompound = false
  Group = -> [Binder,Sketch,Pad,Sketch001,Pad001,Sketch002,Pocket]
  Origin = -> Origin001
  Tip = -> Pocket
FEATURE [App::Part] Part  label="MotorPlatePart"
  Group = -> [Body]
  Origin = -> Origin
COMPONENT P18 — geometry summary ("N20MotorPart"; no construction recipe available for this part):
  bounding box: 39.8 x 18.5 x 12.0 mm
  tessellated surface: 103,723 triangles
  volume: 2845 mm^3 (32% of its bounding box)
COMPONENT P19 — recipe-attached ("WheelPart", a linked part whose construction recipe lives in a companion FreeCAD document of the same project; that document's serialized recipe follows).
Construction recipe (the companion document, serialized — sketch geometry with constraints, then the solid features built on it; lengths are millimeters unless a unit is written):

FCSTD DOCUMENT  (FreeCAD 1.0R39109 (Git))
Label: Wheel
License: All rights reserved
LicenseURL: https://en.wikipedia.org/wiki/All_rights_reserved
objects: Sketcher::SketchObject×5, PartDesign::Pad×4, PartDesign::Pocket×1, PartDesign::Body×1, App::Part×1
note: 26 computed .brp shape members not serialized (recipe doc carries the construction recipe); baked Part::Feature solids carry a one-line shape summary decoded from their .brp

FEATURE [Sketcher::SketchObject] Sketch
  ArcFitTolerance = 1e-06
  AttachmentSupport = -> [YZ_Plane001]
  FullyConstrained = true
  MakeInternals = false
  MapMode = 5
  Placement = pos=(0,0,0) rot=(0.57735,0.57735,0.57735;2.0944rad)
  sketch-geometry (2):
    g0: Circle CenterX=0 CenterY=0 CenterZ=0 NormalX=0 NormalY=0 NormalZ=1 AngleXU=0 Radius=17.5
    g1: Circle CenterX=0 CenterY=0 CenterZ=0 NormalX=0 NormalY=0 NormalZ=1 AngleXU=0 Radius=27.5
  constraints (4):
    c: Diameter(g0) = 35
    c: Coincident(g0,g-1)
    c: Coincident(g1,g0)
    c: Diameter(g1) = 55
FEATURE [PartDesign::Pad] Pad
  Direction = (1,0,0)
  Length = 25
  Length2 = 10
  Placement = pos=(0,0,0) rot=(1,1,1;2.0944rad)
  Profile = -> Sketch
  ReferenceAxis = -> Sketch [N_Axis]
  Refine = true
  Reversed = true
  Suppressed = false
  Type = 0
FEATURE [Sketcher::SketchObject] Sketch001
  ArcFitTolerance = 1e-06
  AttachmentSupport = -> [YZ_Plane001]
  FullyConstrained = true
  MakeInternals = false
  MapMode = 5
  Placement = pos=(0,0,0) rot=(0.57735,0.57735,0.57735;2.0944rad)
  sketch-geometry (9):
    g0: Circle CenterX=0 CenterY=0 CenterZ=0 NormalX=0 NormalY=0 NormalZ=1 AngleXU=0 Radius=17.5
    g1: Circle CenterX=0 CenterY=0 CenterZ=0 NormalX=0 NormalY=0 NormalZ=1 AngleXU=0 Radius=4.55
    g2: LineSegment [constr] StartX=0 StartY=10 StartZ=0 EndX=-8.66025 EndY=-5 EndZ=0
    g3: LineSegment [constr] StartX=-8.66025 StartY=-5 StartZ=0 EndX=8.66025 EndY=-5 EndZ=0
    g4: LineSegment [constr] StartX=8.66025 StartY=-5 StartZ=0 EndX=0 EndY=10 EndZ=0
    g5: Circle [constr] CenterX=0 CenterY=0 CenterZ=0 NormalX=0 NormalY=0 NormalZ=1 AngleXU=0 Radius=10
    g6: Circle CenterX=0 CenterY=10 CenterZ=0 NormalX=0 NormalY=0 NormalZ=1 AngleXU=0 Radius=1.5
    g7: Circle CenterX=-8.66025 CenterY=-5 CenterZ=0 NormalX=0 NormalY=0 NormalZ=1 AngleXU=0 Radius=1.5
    g8: Circle CenterX=8.66025 CenterY=-5 CenterZ=0 NormalX=0 NormalY=0 NormalZ=1 AngleXU=0 Radius=1.5
  constraints (21):
    c: Diameter(g0) = 35
    c: Coincident(g0,g-1)
    c: Diameter(g1) = 9.1
    c: Coincident(g1,g0)
    c: Coincident(g2,g3)
    c: Coincident(g3,g4)
    c: Coincident(g4,g2)
    c: Equal(g2,g3)
    c: Equal(g2,g4)
    c: PointOnObject(g2,g5)
    c: PointOnObject(g3,g5)
    c: PointOnObject(g4,g5)
    c: Coincident(g5,g0)
    c: PointOnObject(g4,g-2)
    c: Diameter(g6) = 3
    c: Coincident(g6,g2)
    c: Diameter(g7) = 3
    c: Coincident(g7,g2)
    c: Diameter(g8) = 3
    c: Coincident(g8,g3)
    c: DistanceY(g0,g2) = 10
FEATURE [PartDesign::Pad] Pad001
  BaseFeature = -> Pad
  Direction = (1,0,0)
  Length = 16
  Length2 = 10
  Placement = pos=(0,0,0) rot=(1,1,1;2.0944rad)
  Profile = -> Sketch001
  ReferenceAxis = -> Sketch001 [N_Axis]
  Refine = true
  Reversed = true
  Suppressed = false
  Type = 0
FEATURE [Sketcher::SketchObject] Sketch002
  ArcFitTolerance = 1e-06
  AttachmentSupport = -> [YZ_Plane001]
  FullyConstrained = true
  MakeInternals = false
  MapMode = 5
  Placement = pos=(0,0,0) rot=(0.57735,0.57735,0.57735;2.0944rad)
  sketch-geometry (1):
    g0: Circle CenterX=0 CenterY=0 CenterZ=0 NormalX=0 NormalY=0 NormalZ=1 AngleXU=0 Radius=17.5
  constraints (2):
    c: Diameter(g0) = 35
    c: Coincident(g0,g-1)
FEATURE [PartDesign::Pocket] Pocket
  BaseFeature = -> Pad001
  Direction = (-1,0,0)
  Length = 13
  Length2 = 5
  Placement = pos=(0,0,0) rot=(1,1,1;2.0944rad)
  Profile = -> Sketch002
  ReferenceAxis = -> Sketch002 [N_Axis]
  Refine = true
  Suppressed = false
  Type = 0
FEATURE [Sketcher::SketchObject] Sketch003
  ArcFitTolerance = 1e-06
  AttachmentSupport = -> [Pocket]
  FullyConstrained = true
  MakeInternals = false
  MapMode = 5
  Placement = pos=(-13,2.9e-15,-1.4e-15) rot=(0.57735,0.57735,0.57735;2.0944rad)
  sketch-geometry (2):
    g0: Circle CenterX=0 CenterY=0 CenterZ=0 NormalX=0 NormalY=0 NormalZ=1 AngleXU=0 Radius=4.55
    g1: Circle CenterX=0 CenterY=0 CenterZ=0 NormalX=0 NormalY=0 NormalZ=1 AngleXU=0 Radius=5.55
  constraints (4):
    c: Diameter(g0) = 9.1
    c: Coincident(g0,g-1)
    c: Coincident(g1,g0)
    c: Diameter(g1) = 11.1
FEATURE [PartDesign::Pad] Pad002
  BaseFeature = -> Pocket
  Direction = (1,0,0)
  Length = 2
  Length2 = 10
  Placement = pos=(0,0,0) rot=(1,1,1;2.0944rad)
  Profile = -> Sketch003
  ReferenceAxis = -> Sketch003 [N_Axis]
  Refine = true
  Suppressed = false
  Type = 0
FEATURE [Sketcher::SketchObject] Sketch004
  ArcFitTolerance = 1e-06
  AttachmentSupport = -> [Pad002]
  FullyConstrained = true
  MakeInternals = false
  MapMode = 5
  Placement = pos=(-16,1.07e-14,-5.3e-15) rot=(0.57735,0.57735,-0.57735;4.18879rad)
  sketch-geometry (2):
    g0: Circle CenterX=0 CenterY=0 CenterZ=0 NormalX=0 NormalY=0 NormalZ=1 AngleXU=0 Radius=4.55
    g1: Circle CenterX=0 CenterY=0 CenterZ=0 NormalX=0 NormalY=0 NormalZ=1 AngleXU=0 Radius=5.55
  constraints (4):
    c: Diameter(g0) = 9.1
    c: Coincident(g0,g-1)
    c: Diameter(g1) = 11.1
    c: Coincident(g1,g0)
FEATURE [PartDesign::Pad] Pad003
  BaseFeature = -> Pad002
  Direction = (-1,0,0)
  Length = 2
  Length2 = 10
  Placement = pos=(0,0,0) rot=(1,1,1;2.0944rad)
  Profile = -> Sketch004
  ReferenceAxis = -> Sketch004 [N_Axis]
  Refine = true
  Suppressed = false
  Type = 0
FEATURE [PartDesign::Body] Body  label="WheelBody"
  AllowCompound = false
  Group = -> [Sketch,Pad,Sketch001,Pad001,Sketch002,Pocket,Sketch003,Pad002,Sketch004,Pad003]
  Origin = -> Origin001
  Tip = -> Pad003
FEATURE [App::Part] Part  label="WheelPart"
  Group = -> [Body]
  Origin = -> Origin
COMPONENT P20 — same part as P19; its construction recipe is shown at P19.
PROVENANCE & LICENSES
A FreeCAD (.FCStd) document from a public repository crawl; recipes are the document's own serialized feature recipes (and, for linked parts, companion documents' recipes).
License: as declared in the source repository (recorded in the dataset sidecar).
